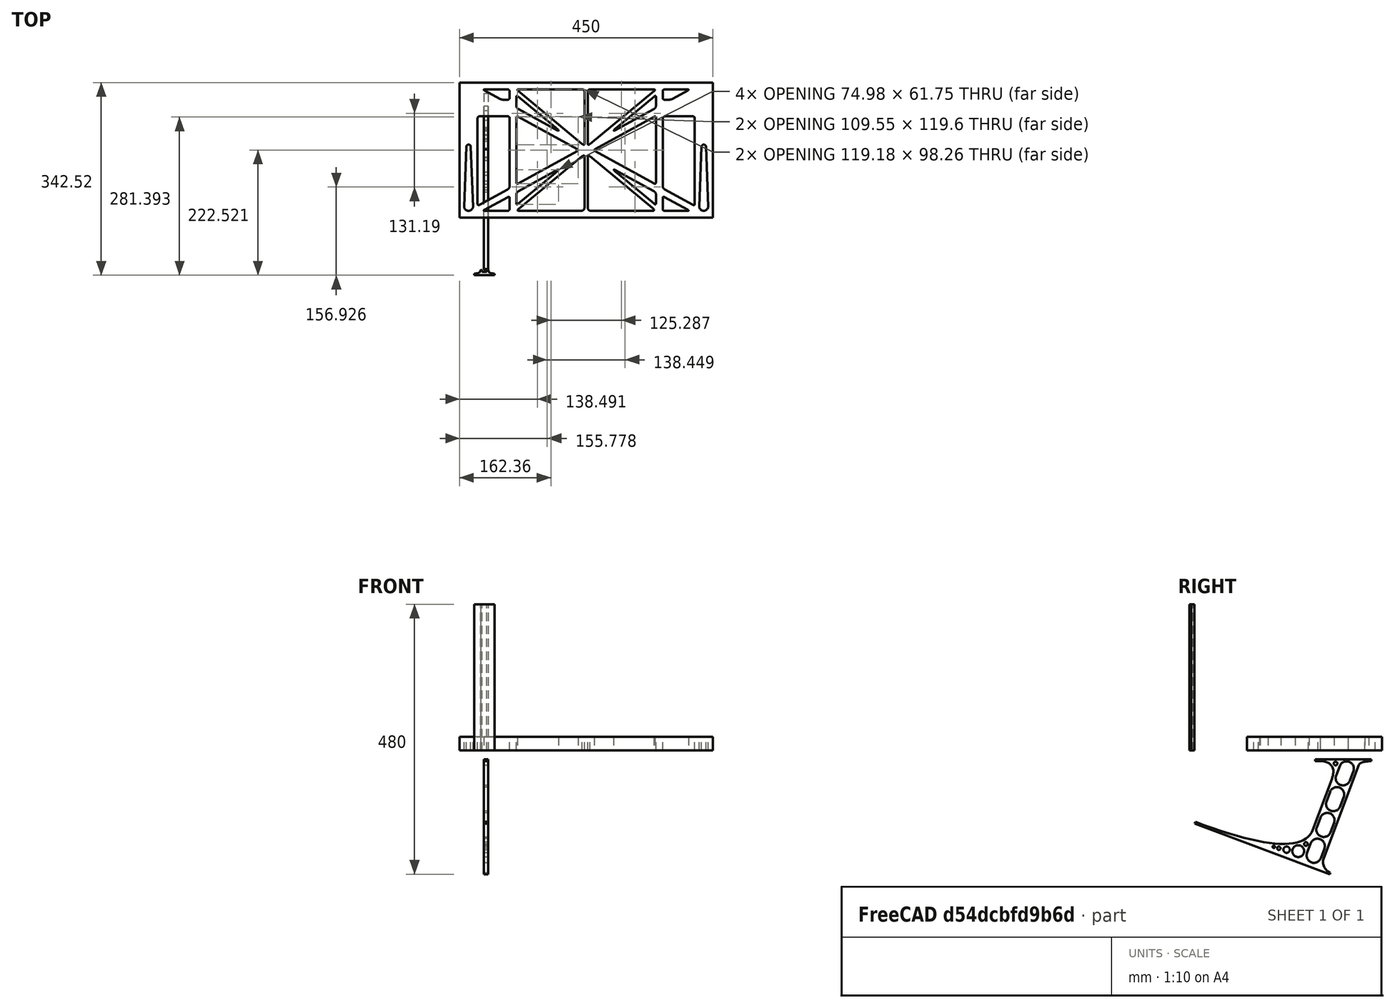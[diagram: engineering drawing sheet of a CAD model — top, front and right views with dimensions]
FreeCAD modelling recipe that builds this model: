
FCSTD DOCUMENT  (FreeCAD 0.19R0.19.2)
Label: laptopStand173FCStd
License: All rights reserved
LicenseURL: http://en.wikipedia.org/wiki/All_rights_reserved
objects: Sketcher::SketchObject×4, Part::Extrusion×3
note: 7 computed .brp shape members not serialized (recipe doc carries the construction recipe); baked Part::Feature solids carry a one-line shape summary decoded from their .brp

FEATURE [Sketcher::SketchObject] Sketch
  FullyConstrained = false
  sketch-geometry (349):
    g0: LineSegment StartX=-10.9272 StartY=-82.7794 StartZ=0 EndX=46.0728 EndY=-51.4823 EndZ=0
    g1: LineSegment StartX=-10.9272 StartY=76.4095 StartZ=0 EndX=-10.9272 EndY=-82.7794 EndZ=0
    g2: LineSegment StartX=46.0728 StartY=76.4095 StartZ=0 EndX=46.0728 EndY=-51.4823 EndZ=0
    g3: LineSegment StartX=-42.9272 StartY=136.221 StartZ=0 EndX=-42.9272 EndY=-103.779 EndZ=0
    g4: LineSegment StartX=407.073 StartY=136.221 StartZ=0 EndX=407.073 EndY=-103.779 EndZ=0
    g5: ArcOfCircle CenterX=-26.9272 CenterY=-83.7794 CenterZ=0 NormalX=0 NormalY=0 NormalZ=1 AngleXU=0 Radius=8 StartAngle=3.14159 EndAngle=6.28319
    g6: ArcOfCircle CenterX=391.073 CenterY=22.1087 CenterZ=0 NormalX=0 NormalY=0 NormalZ=1 AngleXU=0 Radius=8 StartAngle=-4.4e-15 EndAngle=3.14159
    g7: LineSegment StartX=399.073 StartY=22.1087 StartZ=0 EndX=399.073 EndY=-83.7794 EndZ=0
    g8: LineSegment StartX=383.073 StartY=22.1087 StartZ=0 EndX=383.073 EndY=-83.7794 EndZ=0
    g9: ArcOfCircle CenterX=391.073 CenterY=-83.7794 CenterZ=0 NormalX=0 NormalY=0 NormalZ=1 AngleXU=0 Radius=8 StartAngle=3.14159 EndAngle=6.28319
    g10: Circle CenterX=175.022 CenterY=27.0628 CenterZ=0 NormalX=0 NormalY=0 NormalZ=1 AngleXU=0 Radius=1
    g11: Circle CenterX=179.022 CenterY=24.8665 CenterZ=0 NormalX=0 NormalY=0 NormalZ=1 AngleXU=0 Radius=1
    g12: Circle CenterX=179.022 CenterY=27.0628 CenterZ=0 NormalX=0 NormalY=0 NormalZ=1 AngleXU=0 Radius=1
    g13: BSplineCurve PolesCount=3 KnotsCount=2 Degree=2 IsPeriodic=0
    g14: GeomPoint X=175.022 Y=27.0628 Z=0
    g15: GeomPoint X=179.022 Y=27.0628 Z=0
    g16: Circle CenterX=189.124 CenterY=27.0628 CenterZ=0 NormalX=0 NormalY=0 NormalZ=1 AngleXU=0 Radius=1
    g17: Circle CenterX=185.124 CenterY=24.8665 CenterZ=0 NormalX=0 NormalY=0 NormalZ=1 AngleXU=0 Radius=1
    g18: Circle CenterX=185.124 CenterY=27.0628 CenterZ=0 NormalX=0 NormalY=0 NormalZ=1 AngleXU=0 Radius=1
    g19: BSplineCurve PolesCount=3 KnotsCount=2 Degree=2 IsPeriodic=0
    g20: GeomPoint X=189.124 Y=27.0628 Z=0
    g21: GeomPoint X=185.124 Y=27.0628 Z=0
    g22: Circle CenterX=175.022 CenterY=5.37834 CenterZ=0 NormalX=0 NormalY=0 NormalZ=1 AngleXU=0 Radius=1
    g23: Circle CenterX=179.022 CenterY=7.57463 CenterZ=0 NormalX=0 NormalY=0 NormalZ=1 AngleXU=0 Radius=1
    g24: Circle CenterX=179.022 CenterY=5.34704 CenterZ=0 NormalX=0 NormalY=0 NormalZ=1 AngleXU=0 Radius=1
    g25: BSplineCurve PolesCount=3 KnotsCount=2 Degree=2 IsPeriodic=0
    g26: GeomPoint X=175.022 Y=5.37834 Z=0
    g27: GeomPoint X=179.022 Y=5.34704 Z=0
    g28: Circle CenterX=189.124 CenterY=5.37834 CenterZ=0 NormalX=0 NormalY=0 NormalZ=1 AngleXU=0 Radius=1
    g29: Circle CenterX=185.124 CenterY=7.57463 CenterZ=0 NormalX=0 NormalY=0 NormalZ=1 AngleXU=0 Radius=1
    g30: Circle CenterX=185.124 CenterY=5.34704 CenterZ=0 NormalX=0 NormalY=0 NormalZ=1 AngleXU=0 Radius=1
    g31: BSplineCurve PolesCount=3 KnotsCount=2 Degree=2 IsPeriodic=0
    g32: GeomPoint X=189.124 Y=5.37834 Z=0
    g33: GeomPoint X=185.124 Y=5.34704 Z=0
    g34: Circle CenterX=165.871 CenterY=18.1458 CenterZ=0 NormalX=0 NormalY=0 NormalZ=1 AngleXU=0 Radius=1
    g35: Circle CenterX=169.377 CenterY=16.2206 CenterZ=0 NormalX=0 NormalY=0 NormalZ=1 AngleXU=0 Radius=1
    g36: Circle CenterX=165.871 CenterY=14.2954 CenterZ=0 NormalX=0 NormalY=0 NormalZ=1 AngleXU=0 Radius=1
    g37: BSplineCurve PolesCount=3 KnotsCount=2 Degree=2 IsPeriodic=0
    g38: GeomPoint X=165.871 Y=18.1458 Z=0
    g39: GeomPoint X=165.871 Y=14.2954 Z=0
    g40: Circle CenterX=198.275 CenterY=18.1458 CenterZ=0 NormalX=0 NormalY=0 NormalZ=1 AngleXU=0 Radius=1
    g41: Circle CenterX=194.768 CenterY=16.2206 CenterZ=0 NormalX=0 NormalY=0 NormalZ=1 AngleXU=0 Radius=1
    g42: Circle CenterX=198.275 CenterY=14.2954 CenterZ=0 NormalX=0 NormalY=0 NormalZ=1 AngleXU=0 Radius=1
    g43: BSplineCurve PolesCount=3 KnotsCount=2 Degree=2 IsPeriodic=0
    g44: GeomPoint X=198.275 Y=18.1458 Z=0
    g45: GeomPoint X=198.275 Y=14.2954 Z=0
    g46: LineSegment StartX=407.073 StartY=-103.779 StartZ=0 EndX=-42.9272 EndY=-103.779 EndZ=0
    g47: LineSegment StartX=407.073 StartY=136.221 StartZ=0 EndX=-42.9272 EndY=136.221 EndZ=0
    g48: LineSegment StartX=46.0728 StartY=76.4095 StartZ=0 EndX=-10.9272 EndY=76.4095 EndZ=0
    g49: Circle CenterX=125.607 CenterY=54.1951 CenterZ=0 NormalX=0 NormalY=0 NormalZ=1 AngleXU=0 Radius=1
    g50: Circle CenterX=139.632 CenterY=46.4944 CenterZ=0 NormalX=0 NormalY=0 NormalZ=1 AngleXU=0 Radius=1
    g51: Circle CenterX=127.326 CenterY=56.7187 CenterZ=0 NormalX=0 NormalY=0 NormalZ=1 AngleXU=0 Radius=1
    g52: BSplineCurve PolesCount=3 KnotsCount=2 Degree=2 IsPeriodic=0
    g53: GeomPoint X=125.607 Y=54.1951 Z=0
    g54: GeomPoint X=127.326 Y=56.7187 Z=0
    g55: Circle CenterX=236.821 CenterY=56.7187 CenterZ=0 NormalX=0 NormalY=0 NormalZ=1 AngleXU=0 Radius=1
    g56: Circle CenterX=224.513 CenterY=46.4944 CenterZ=0 NormalX=0 NormalY=0 NormalZ=1 AngleXU=0 Radius=1
    g57: Circle CenterX=238.538 CenterY=54.1951 CenterZ=0 NormalX=0 NormalY=0 NormalZ=1 AngleXU=0 Radius=1
    g58: BSplineCurve PolesCount=3 KnotsCount=2 Degree=2 IsPeriodic=0
    g59: GeomPoint X=236.821 Y=56.7187 Z=0
    g60: GeomPoint X=238.538 Y=54.1951 Z=0
    g61: Circle CenterX=238.538 CenterY=-21.7539 CenterZ=0 NormalX=0 NormalY=0 NormalZ=1 AngleXU=0 Radius=1
    g62: Circle CenterX=224.513 CenterY=-14.0532 CenterZ=0 NormalX=0 NormalY=0 NormalZ=1 AngleXU=0 Radius=1
    g63: Circle CenterX=236.821 CenterY=-24.2775 CenterZ=0 NormalX=0 NormalY=0 NormalZ=1 AngleXU=0 Radius=1
    g64: BSplineCurve PolesCount=3 KnotsCount=2 Degree=2 IsPeriodic=0
    g65: GeomPoint X=238.538 Y=-21.7539 Z=0
    g66: GeomPoint X=236.821 Y=-24.2775 Z=0
    g67: Circle CenterX=125.607 CenterY=-21.7539 CenterZ=0 NormalX=0 NormalY=0 NormalZ=1 AngleXU=0 Radius=1
    g68: Circle CenterX=139.632 CenterY=-14.0532 CenterZ=0 NormalX=0 NormalY=0 NormalZ=1 AngleXU=0 Radius=1
    g69: Circle CenterX=127.325 CenterY=-24.2775 CenterZ=0 NormalX=0 NormalY=0 NormalZ=1 AngleXU=0 Radius=1
    g70: BSplineCurve PolesCount=3 KnotsCount=2 Degree=2 IsPeriodic=0
    g71: GeomPoint X=125.607 Y=-21.7539 Z=0
    g72: GeomPoint X=127.325 Y=-24.2775 Z=0
    g73: Circle CenterX=302.996 CenterY=111.695 CenterZ=0 NormalX=0 NormalY=0 NormalZ=1 AngleXU=0 Radius=1
    g74: Circle CenterX=306.073 CenterY=114.251 CenterZ=0 NormalX=0 NormalY=0 NormalZ=1 AngleXU=0 Radius=1
    g75: Circle CenterX=306.073 CenterY=110.251 CenterZ=0 NormalX=0 NormalY=0 NormalZ=1 AngleXU=0 Radius=1
    g76: BSplineCurve PolesCount=3 KnotsCount=2 Degree=2 IsPeriodic=0
    g77: GeomPoint X=302.996 Y=111.695 Z=0
    g78: GeomPoint X=306.073 Y=110.251 Z=0
    g79: Circle CenterX=306.073 CenterY=95.2763 CenterZ=0 NormalX=0 NormalY=0 NormalZ=1 AngleXU=0 Radius=1
    g80: Circle CenterX=306.073 CenterY=91.2763 CenterZ=0 NormalX=0 NormalY=0 NormalZ=1 AngleXU=0 Radius=1
    g81: Circle CenterX=302.567 CenterY=89.3511 CenterZ=0 NormalX=0 NormalY=0 NormalZ=1 AngleXU=0 Radius=1
    g82: BSplineCurve PolesCount=3 KnotsCount=2 Degree=2 IsPeriodic=0
    g83: GeomPoint X=306.073 Y=95.2763 Z=0
    g84: GeomPoint X=302.567 Y=89.3511 Z=0
    g85: LineSegment StartX=306.073 StartY=110.251 StartZ=0 EndX=306.073 EndY=95.2763 EndZ=0
    g86: LineSegment StartX=302.996 StartY=111.695 StartZ=0 EndX=236.821 EndY=56.7187 EndZ=0
    g87: LineSegment StartX=238.538 StartY=54.1951 StartZ=0 EndX=302.567 EndY=89.3511 EndZ=0
    g88: Circle CenterX=61.1496 CenterY=111.695 CenterZ=0 NormalX=0 NormalY=0 NormalZ=1 AngleXU=0 Radius=1
    g89: Circle CenterX=58.0728 CenterY=114.251 CenterZ=0 NormalX=0 NormalY=0 NormalZ=1 AngleXU=0 Radius=1
    g90: Circle CenterX=58.0728 CenterY=110.251 CenterZ=0 NormalX=0 NormalY=0 NormalZ=1 AngleXU=0 Radius=1
    g91: BSplineCurve PolesCount=3 KnotsCount=2 Degree=2 IsPeriodic=0
    g92: GeomPoint X=61.1496 Y=111.695 Z=0
    g93: GeomPoint X=58.0728 Y=110.251 Z=0
    g94: Circle CenterX=61.5791 CenterY=89.3511 CenterZ=0 NormalX=0 NormalY=0 NormalZ=1 AngleXU=0 Radius=1
    g95: Circle CenterX=58.0728 CenterY=91.2763 CenterZ=0 NormalX=0 NormalY=0 NormalZ=1 AngleXU=0 Radius=1
    g96: Circle CenterX=58.0728 CenterY=95.2763 CenterZ=0 NormalX=0 NormalY=0 NormalZ=1 AngleXU=0 Radius=1
    g97: BSplineCurve PolesCount=3 KnotsCount=2 Degree=2 IsPeriodic=0
    g98: GeomPoint X=61.5791 Y=89.3511 Z=0
    g99: GeomPoint X=58.0728 Y=95.2763 Z=0
    g100: LineSegment StartX=58.0728 StartY=110.251 StartZ=0 EndX=58.0728 EndY=95.2763 EndZ=0
    g101: LineSegment StartX=61.1496 StartY=111.695 StartZ=0 EndX=127.326 EndY=56.7187 EndZ=0
    g102: LineSegment StartX=125.607 StartY=54.1951 StartZ=0 EndX=61.5791 EndY=89.3511 EndZ=0
    g103: Circle CenterX=61.5791 CenterY=-56.9099 CenterZ=0 NormalX=0 NormalY=0 NormalZ=1 AngleXU=0 Radius=1
    g104: Circle CenterX=58.0728 CenterY=-58.8351 CenterZ=0 NormalX=0 NormalY=0 NormalZ=1 AngleXU=0 Radius=1
    g105: Circle CenterX=58.0728 CenterY=-62.8351 CenterZ=0 NormalX=0 NormalY=0 NormalZ=1 AngleXU=0 Radius=1
    g106: BSplineCurve PolesCount=3 KnotsCount=2 Degree=2 IsPeriodic=0
    g107: GeomPoint X=61.5791 Y=-56.9099 Z=0
    g108: GeomPoint X=58.0728 Y=-62.8351 Z=0
    g109: Circle CenterX=58.0728 CenterY=-77.8102 CenterZ=0 NormalX=0 NormalY=0 NormalZ=1 AngleXU=0 Radius=1
    g110: Circle CenterX=58.0728 CenterY=-81.8102 CenterZ=0 NormalX=0 NormalY=0 NormalZ=1 AngleXU=0 Radius=1
    g111: Circle CenterX=61.1496 CenterY=-79.2541 CenterZ=0 NormalX=0 NormalY=0 NormalZ=1 AngleXU=0 Radius=1
    g112: BSplineCurve PolesCount=3 KnotsCount=2 Degree=2 IsPeriodic=0
    g113: GeomPoint X=58.0728 Y=-77.8102 Z=0
    g114: GeomPoint X=61.1496 Y=-79.2541 Z=0
    g115: LineSegment StartX=58.0728 StartY=-62.8351 StartZ=0 EndX=58.0728 EndY=-77.8102 EndZ=0
    g116: LineSegment StartX=61.1496 StartY=-79.2541 StartZ=0 EndX=127.325 EndY=-24.2775 EndZ=0
    g117: LineSegment StartX=125.607 StartY=-21.7539 StartZ=0 EndX=61.5791 EndY=-56.9099 EndZ=0
    g118: Circle CenterX=302.567 CenterY=-56.9099 CenterZ=0 NormalX=0 NormalY=0 NormalZ=1 AngleXU=0 Radius=1
    g119: Circle CenterX=306.073 CenterY=-58.8351 CenterZ=0 NormalX=0 NormalY=0 NormalZ=1 AngleXU=0 Radius=1
    g120: Circle CenterX=306.073 CenterY=-62.8351 CenterZ=0 NormalX=0 NormalY=0 NormalZ=1 AngleXU=0 Radius=1
    g121: BSplineCurve PolesCount=3 KnotsCount=2 Degree=2 IsPeriodic=0
    g122: GeomPoint X=302.567 Y=-56.9099 Z=0
    g123: GeomPoint X=306.073 Y=-62.8351 Z=0
    g124: Circle CenterX=302.996 CenterY=-79.2541 CenterZ=0 NormalX=0 NormalY=0 NormalZ=1 AngleXU=0 Radius=1
    g125: Circle CenterX=306.073 CenterY=-81.8102 CenterZ=0 NormalX=0 NormalY=0 NormalZ=1 AngleXU=0 Radius=1
    g126: Circle CenterX=306.073 CenterY=-77.8102 CenterZ=0 NormalX=0 NormalY=0 NormalZ=1 AngleXU=0 Radius=1
    g127: BSplineCurve PolesCount=3 KnotsCount=2 Degree=2 IsPeriodic=0
    g128: GeomPoint X=302.996 Y=-79.2541 Z=0
    g129: GeomPoint X=306.073 Y=-77.8102 Z=0
    g130: LineSegment StartX=306.073 StartY=-62.8351 StartZ=0 EndX=306.073 EndY=-77.8102 EndZ=0
    g131: LineSegment StartX=302.996 StartY=-79.2541 StartZ=0 EndX=236.821 EndY=-24.2775 EndZ=0
    g132: LineSegment StartX=238.538 StartY=-21.7539 StartZ=0 EndX=302.567 EndY=-56.9099 EndZ=0
    g133: Circle CenterX=61.6457 CenterY=-88.8112 CenterZ=0 NormalX=0 NormalY=0 NormalZ=1 AngleXU=0 Radius=1
    g134: Circle CenterX=58.0728 CenterY=-91.7794 CenterZ=0 NormalX=0 NormalY=0 NormalZ=1 AngleXU=0 Radius=1
    g135: Circle CenterX=63.9135 CenterY=-91.7794 CenterZ=0 NormalX=0 NormalY=0 NormalZ=1 AngleXU=0 Radius=1
    g136: BSplineCurve PolesCount=3 KnotsCount=2 Degree=2 IsPeriodic=0
    g137: GeomPoint X=61.6457 Y=-88.8112 Z=0
    g138: GeomPoint X=63.9135 Y=-91.7794 Z=0
    g139: Circle CenterX=179.022 CenterY=-85.8163 CenterZ=0 NormalX=0 NormalY=0 NormalZ=1 AngleXU=0 Radius=1
    g140: Circle CenterX=179.022 CenterY=-91.7794 CenterZ=0 NormalX=0 NormalY=0 NormalZ=1 AngleXU=0 Radius=1
    g141: Circle CenterX=171.895 CenterY=-91.7794 CenterZ=0 NormalX=0 NormalY=0 NormalZ=1 AngleXU=0 Radius=1
    g142: BSplineCurve PolesCount=3 KnotsCount=2 Degree=2 IsPeriodic=0
    g143: GeomPoint X=179.022 Y=-85.8163 Z=0
    g144: GeomPoint X=171.895 Y=-91.7794 Z=0
    g145: Circle CenterX=185.124 CenterY=-86.2028 CenterZ=0 NormalX=0 NormalY=0 NormalZ=1 AngleXU=0 Radius=1
    g146: Circle CenterX=185.124 CenterY=-91.7794 CenterZ=0 NormalX=0 NormalY=0 NormalZ=1 AngleXU=0 Radius=1
    g147: Circle CenterX=191.747 CenterY=-91.7794 CenterZ=0 NormalX=0 NormalY=0 NormalZ=1 AngleXU=0 Radius=1
    g148: BSplineCurve PolesCount=3 KnotsCount=2 Degree=2 IsPeriodic=0
    g149: GeomPoint X=185.124 Y=-86.2028 Z=0
    g150: GeomPoint X=191.747 Y=-91.7794 Z=0
    g151: Circle CenterX=299.888 CenterY=-86.6413 CenterZ=0 NormalX=0 NormalY=0 NormalZ=1 AngleXU=0 Radius=1
    g152: Circle CenterX=306.073 CenterY=-91.7794 CenterZ=0 NormalX=0 NormalY=0 NormalZ=1 AngleXU=0 Radius=1
    g153: Circle CenterX=298.776 CenterY=-91.7794 CenterZ=0 NormalX=0 NormalY=0 NormalZ=1 AngleXU=0 Radius=1
    g154: BSplineCurve PolesCount=3 KnotsCount=2 Degree=2 IsPeriodic=0
    g155: GeomPoint X=299.888 Y=-86.6413 Z=0
    g156: GeomPoint X=298.776 Y=-91.7794 Z=0
    g157: LineSegment StartX=189.124 StartY=5.37834 StartZ=0 EndX=299.888 EndY=-86.6413 EndZ=0
    g158: LineSegment StartX=298.776 StartY=-91.7794 StartZ=0 EndX=191.747 EndY=-91.7794 EndZ=0
    g159: LineSegment StartX=185.124 StartY=-86.2028 StartZ=0 EndX=185.124 EndY=5.34704 EndZ=0
    g160: LineSegment StartX=179.022 StartY=5.34704 StartZ=0 EndX=179.022 EndY=-85.8163 EndZ=0
    g161: LineSegment StartX=171.895 StartY=-91.7794 StartZ=0 EndX=63.9135 EndY=-91.7794 EndZ=0
    g162: LineSegment StartX=61.6457 StartY=-88.8112 StartZ=0 EndX=175.022 EndY=5.37834 EndZ=0
    g163: Circle CenterX=302.073 CenterY=124.221 CenterZ=0 NormalX=0 NormalY=0 NormalZ=1 AngleXU=0 Radius=1
    g164: Circle CenterX=306.073 CenterY=124.221 CenterZ=0 NormalX=0 NormalY=0 NormalZ=1 AngleXU=0 Radius=1
    g165: Circle CenterX=302.996 CenterY=121.665 CenterZ=0 NormalX=0 NormalY=0 NormalZ=1 AngleXU=0 Radius=1
    g166: BSplineCurve PolesCount=3 KnotsCount=2 Degree=2 IsPeriodic=0
    g167: GeomPoint X=302.073 Y=124.221 Z=0
    g168: GeomPoint X=302.996 Y=121.665 Z=0
    g169: Circle CenterX=189.124 CenterY=124.221 CenterZ=0 NormalX=0 NormalY=0 NormalZ=1 AngleXU=0 Radius=1
    g170: Circle CenterX=185.124 CenterY=124.221 CenterZ=0 NormalX=0 NormalY=0 NormalZ=1 AngleXU=0 Radius=1
    g171: Circle CenterX=185.124 CenterY=120.221 CenterZ=0 NormalX=0 NormalY=0 NormalZ=1 AngleXU=0 Radius=1
    g172: BSplineCurve PolesCount=3 KnotsCount=2 Degree=2 IsPeriodic=0
    g173: GeomPoint X=189.124 Y=124.221 Z=0
    g174: GeomPoint X=185.124 Y=120.221 Z=0
    g175: Circle CenterX=175.022 CenterY=124.221 CenterZ=0 NormalX=0 NormalY=0 NormalZ=1 AngleXU=0 Radius=1
    g176: Circle CenterX=179.022 CenterY=124.221 CenterZ=0 NormalX=0 NormalY=0 NormalZ=1 AngleXU=0 Radius=1
    g177: Circle CenterX=179.022 CenterY=120.221 CenterZ=0 NormalX=0 NormalY=0 NormalZ=1 AngleXU=0 Radius=1
    g178: BSplineCurve PolesCount=3 KnotsCount=2 Degree=2 IsPeriodic=0
    g179: GeomPoint X=175.022 Y=124.221 Z=0
    g180: GeomPoint X=179.022 Y=120.221 Z=0
    g181: Circle CenterX=62.0728 CenterY=124.221 CenterZ=0 NormalX=0 NormalY=0 NormalZ=1 AngleXU=0 Radius=1
    g182: Circle CenterX=58.0728 CenterY=124.221 CenterZ=0 NormalX=0 NormalY=0 NormalZ=1 AngleXU=0 Radius=1
    g183: Circle CenterX=61.1496 CenterY=121.665 CenterZ=0 NormalX=0 NormalY=0 NormalZ=1 AngleXU=0 Radius=1
    g184: BSplineCurve PolesCount=3 KnotsCount=2 Degree=2 IsPeriodic=0
    g185: GeomPoint X=62.0728 Y=124.221 Z=0
    g186: GeomPoint X=61.1496 Y=121.665 Z=0
    g187: LineSegment StartX=62.0728 StartY=124.221 StartZ=0 EndX=175.022 EndY=124.221 EndZ=0
    g188: LineSegment StartX=179.022 StartY=120.221 StartZ=0 EndX=179.022 EndY=27.0628 EndZ=0
    g189: LineSegment StartX=185.124 StartY=27.0628 StartZ=0 EndX=185.124 EndY=120.221 EndZ=0
    g190: LineSegment StartX=189.124 StartY=124.221 StartZ=0 EndX=302.073 EndY=124.221 EndZ=0
    g191: LineSegment StartX=302.996 StartY=121.665 StartZ=0 EndX=189.124 EndY=27.0628 EndZ=0
    g192: LineSegment StartX=175.022 StartY=27.0628 StartZ=0 EndX=61.1496 EndY=121.665 EndZ=0
    g193: Circle CenterX=61.5791 CenterY=75.4095 CenterZ=0 NormalX=0 NormalY=0 NormalZ=1 AngleXU=0 Radius=1
    g194: Circle CenterX=58.0728 CenterY=77.3346 CenterZ=0 NormalX=0 NormalY=0 NormalZ=1 AngleXU=0 Radius=1
    g195: Circle CenterX=58.0728 CenterY=73.3346 CenterZ=0 NormalX=0 NormalY=0 NormalZ=1 AngleXU=0 Radius=1
    g196: BSplineCurve PolesCount=3 KnotsCount=2 Degree=2 IsPeriodic=0
    g197: GeomPoint X=61.5791 Y=75.4095 Z=0
    g198: GeomPoint X=58.0728 Y=73.3346 Z=0
    g199: Circle CenterX=58.0728 CenterY=-40.8935 CenterZ=0 NormalX=0 NormalY=0 NormalZ=1 AngleXU=0 Radius=1
    g200: Circle CenterX=58.0728 CenterY=-44.8935 CenterZ=0 NormalX=0 NormalY=0 NormalZ=1 AngleXU=0 Radius=1
    g201: Circle CenterX=61.5791 CenterY=-42.9683 CenterZ=0 NormalX=0 NormalY=0 NormalZ=1 AngleXU=0 Radius=1
    g202: BSplineCurve PolesCount=3 KnotsCount=2 Degree=2 IsPeriodic=0
    g203: GeomPoint X=58.0728 Y=-40.8935 Z=0
    g204: GeomPoint X=61.5791 Y=-42.9683 Z=0
    g205: LineSegment StartX=61.5791 StartY=-42.9683 StartZ=0 EndX=165.871 EndY=14.2954 EndZ=0
    g206: LineSegment StartX=165.871 StartY=18.1458 StartZ=0 EndX=61.5791 EndY=75.4095 EndZ=0
    g207: LineSegment StartX=58.0728 StartY=73.3346 StartZ=0 EndX=58.0728 EndY=-40.8935 EndZ=0
    g208: Circle CenterX=302.567 CenterY=-42.9683 CenterZ=0 NormalX=0 NormalY=0 NormalZ=1 AngleXU=0 Radius=1
    g209: Circle CenterX=306.073 CenterY=-44.8935 CenterZ=0 NormalX=0 NormalY=0 NormalZ=1 AngleXU=0 Radius=1
    g210: Circle CenterX=306.073 CenterY=-40.8935 CenterZ=0 NormalX=0 NormalY=0 NormalZ=1 AngleXU=0 Radius=1
    g211: BSplineCurve PolesCount=3 KnotsCount=2 Degree=2 IsPeriodic=0
    g212: GeomPoint X=302.567 Y=-42.9683 Z=0
    g213: GeomPoint X=306.073 Y=-40.8935 Z=0
    g214: Circle CenterX=306.073 CenterY=73.3346 CenterZ=0 NormalX=0 NormalY=0 NormalZ=1 AngleXU=0 Radius=1
    g215: Circle CenterX=306.073 CenterY=77.3346 CenterZ=0 NormalX=0 NormalY=0 NormalZ=1 AngleXU=0 Radius=1
    g216: Circle CenterX=302.567 CenterY=75.4095 CenterZ=0 NormalX=0 NormalY=0 NormalZ=1 AngleXU=0 Radius=1
    g217: BSplineCurve PolesCount=3 KnotsCount=2 Degree=2 IsPeriodic=0
    g218: GeomPoint X=306.073 Y=73.3346 Z=0
    g219: GeomPoint X=302.567 Y=75.4095 Z=0
    g220: LineSegment StartX=302.567 StartY=-42.9683 StartZ=0 EndX=198.275 EndY=14.2954 EndZ=0
    g221: LineSegment StartX=198.275 StartY=18.1458 StartZ=0 EndX=302.567 EndY=75.4095 EndZ=0
    g222: LineSegment StartX=306.073 StartY=73.3346 StartZ=0 EndX=306.073 EndY=-40.8935 EndZ=0
    g223: LineSegment StartX=322.073 StartY=105.865 StartZ=0 EndX=328.643 EndY=105.865 EndZ=0
    g224: LineSegment StartX=318.073 StartY=120.221 StartZ=0 EndX=318.073 EndY=109.865 EndZ=0
    g225: LineSegment StartX=336.157 StartY=107.779 StartZ=0 EndX=362.567 EndY=122.294 EndZ=0
    g226: Circle CenterX=362.073 CenterY=124.221 CenterZ=0 NormalX=0 NormalY=0 NormalZ=1 AngleXU=0 Radius=1
    g227: Circle CenterX=366.073 CenterY=124.221 CenterZ=0 NormalX=0 NormalY=0 NormalZ=1 AngleXU=0 Radius=1
    g228: Circle CenterX=362.567 CenterY=122.294 CenterZ=0 NormalX=0 NormalY=0 NormalZ=1 AngleXU=0 Radius=1
    g229: BSplineCurve PolesCount=3 KnotsCount=2 Degree=2 IsPeriodic=0
    g230: GeomPoint X=362.073 Y=124.221 Z=0
    g231: GeomPoint X=362.567 Y=122.294 Z=0
    g232: Circle CenterX=322.073 CenterY=124.221 CenterZ=0 NormalX=0 NormalY=0 NormalZ=1 AngleXU=0 Radius=1
    g233: Circle CenterX=318.073 CenterY=124.221 CenterZ=0 NormalX=0 NormalY=0 NormalZ=1 AngleXU=0 Radius=1
    g234: Circle CenterX=318.073 CenterY=120.221 CenterZ=0 NormalX=0 NormalY=0 NormalZ=1 AngleXU=0 Radius=1
    g235: BSplineCurve PolesCount=3 KnotsCount=2 Degree=2 IsPeriodic=0
    g236: GeomPoint X=322.073 Y=124.221 Z=0
    g237: GeomPoint X=318.073 Y=120.221 Z=0
    g238: Circle CenterX=322.073 CenterY=105.865 CenterZ=0 NormalX=0 NormalY=0 NormalZ=1 AngleXU=0 Radius=1
    g239: Circle CenterX=318.073 CenterY=105.865 CenterZ=0 NormalX=0 NormalY=0 NormalZ=1 AngleXU=0 Radius=1
    g240: Circle CenterX=318.073 CenterY=109.865 CenterZ=0 NormalX=0 NormalY=0 NormalZ=1 AngleXU=0 Radius=1
    g241: BSplineCurve PolesCount=3 KnotsCount=2 Degree=2 IsPeriodic=0
    g242: GeomPoint X=322.073 Y=105.865 Z=0
    g243: GeomPoint X=318.073 Y=109.865 Z=0
    g244: Circle CenterX=336.157 CenterY=107.779 CenterZ=0 NormalX=0 NormalY=0 NormalZ=1 AngleXU=0 Radius=1
    g245: Circle CenterX=332.651 CenterY=105.853 CenterZ=0 NormalX=0 NormalY=0 NormalZ=1 AngleXU=0 Radius=1
    g246: Circle CenterX=328.643 CenterY=105.865 CenterZ=0 NormalX=0 NormalY=0 NormalZ=1 AngleXU=0 Radius=1
    g247: BSplineCurve PolesCount=3 KnotsCount=2 Degree=2 IsPeriodic=0
    g248: GeomPoint X=336.157 Y=107.779 Z=0
    g249: GeomPoint X=328.643 Y=105.865 Z=0
    g250: LineSegment StartX=322.073 StartY=124.221 StartZ=0 EndX=362.073 EndY=124.221 EndZ=0
    g251: Circle CenterX=371.567 CenterY=-80.8644 CenterZ=0 NormalX=0 NormalY=0 NormalZ=1 AngleXU=0 Radius=1
    g252: Circle CenterX=375.073 CenterY=-82.7896 CenterZ=0 NormalX=0 NormalY=0 NormalZ=1 AngleXU=0 Radius=1
    g253: Circle CenterX=375.073 CenterY=-78.7896 CenterZ=0 NormalX=0 NormalY=0 NormalZ=1 AngleXU=0 Radius=1
    g254: BSplineCurve PolesCount=3 KnotsCount=2 Degree=2 IsPeriodic=0
    g255: GeomPoint X=371.567 Y=-80.8644 Z=0
    g256: GeomPoint X=375.073 Y=-78.7896 Z=0
    g257: Circle CenterX=321.579 CenterY=-53.4075 CenterZ=0 NormalX=0 NormalY=0 NormalZ=1 AngleXU=0 Radius=1
    g258: Circle CenterX=318.073 CenterY=-51.4823 CenterZ=0 NormalX=0 NormalY=0 NormalZ=1 AngleXU=0 Radius=1
    g259: Circle CenterX=318.073 CenterY=-47.4805 CenterZ=0 NormalX=0 NormalY=0 NormalZ=1 AngleXU=0 Radius=1
    g260: BSplineCurve PolesCount=3 KnotsCount=2 Degree=2 IsPeriodic=0
    g261: GeomPoint X=321.579 Y=-53.4075 Z=0
    g262: GeomPoint X=318.073 Y=-47.4805 Z=0
    g263: LineSegment StartX=371.567 StartY=-80.8644 StartZ=0 EndX=321.579 EndY=-53.4075 EndZ=0
    g264: Circle CenterX=321.579 CenterY=-67.3492 CenterZ=0 NormalX=0 NormalY=0 NormalZ=1 AngleXU=0 Radius=1
    g265: Circle CenterX=318.073 CenterY=-65.424 CenterZ=0 NormalX=0 NormalY=0 NormalZ=1 AngleXU=0 Radius=1
    g266: Circle CenterX=318.073 CenterY=-69.424 CenterZ=0 NormalX=0 NormalY=0 NormalZ=1 AngleXU=0 Radius=1
    g267: BSplineCurve PolesCount=3 KnotsCount=2 Degree=2 IsPeriodic=0
    g268: GeomPoint X=321.579 Y=-67.3492 Z=0
    g269: GeomPoint X=318.073 Y=-69.424 Z=0
    g270: Circle CenterX=362.567 CenterY=-89.8542 CenterZ=0 NormalX=0 NormalY=0 NormalZ=1 AngleXU=0 Radius=1
    g271: Circle CenterX=366.073 CenterY=-91.7794 CenterZ=0 NormalX=0 NormalY=0 NormalZ=1 AngleXU=0 Radius=1
    g272: Circle CenterX=362.073 CenterY=-91.7794 CenterZ=0 NormalX=0 NormalY=0 NormalZ=1 AngleXU=0 Radius=1
    g273: BSplineCurve PolesCount=3 KnotsCount=2 Degree=2 IsPeriodic=0
    g274: GeomPoint X=362.567 Y=-89.8542 Z=0
    g275: GeomPoint X=362.073 Y=-91.7794 Z=0
    g276: Circle CenterX=322.073 CenterY=-91.7794 CenterZ=0 NormalX=0 NormalY=0 NormalZ=1 AngleXU=0 Radius=1
    g277: Circle CenterX=318.073 CenterY=-91.7794 CenterZ=0 NormalX=0 NormalY=0 NormalZ=1 AngleXU=0 Radius=1
    g278: Circle CenterX=318.073 CenterY=-87.7794 CenterZ=0 NormalX=0 NormalY=0 NormalZ=1 AngleXU=0 Radius=1
    g279: BSplineCurve PolesCount=3 KnotsCount=2 Degree=2 IsPeriodic=0
    g280: GeomPoint X=322.073 Y=-91.7794 Z=0
    g281: GeomPoint X=318.073 Y=-87.7794 Z=0
    g282: LineSegment StartX=362.567 StartY=-89.8542 StartZ=0 EndX=321.579 EndY=-67.3492 EndZ=0
    g283: LineSegment StartX=318.073 StartY=-69.424 StartZ=0 EndX=318.073 EndY=-87.7794 EndZ=0
    g284: LineSegment StartX=322.073 StartY=-91.7794 StartZ=0 EndX=362.073 EndY=-91.7794 EndZ=0
    g285: Circle CenterX=2.07281 CenterY=124.221 CenterZ=0 NormalX=0 NormalY=0 NormalZ=1 AngleXU=0 Radius=1
    g286: Circle CenterX=1.57905 CenterY=122.295 CenterZ=0 NormalX=0 NormalY=0 NormalZ=1 AngleXU=0 Radius=1
    g287: BSplineCurve PolesCount=3 KnotsCount=2 Degree=2 IsPeriodic=0
    g288: GeomPoint X=2.07281 Y=124.221 Z=0
    g289: GeomPoint X=1.57905 Y=122.295 Z=0
    g290: Circle CenterX=42.0728 CenterY=124.221 CenterZ=0 NormalX=0 NormalY=0 NormalZ=1 AngleXU=0 Radius=1
    g291: Circle CenterX=46.0728 CenterY=124.221 CenterZ=0 NormalX=0 NormalY=0 NormalZ=1 AngleXU=0 Radius=1
    g292: Circle CenterX=46.0728 CenterY=120.221 CenterZ=0 NormalX=0 NormalY=0 NormalZ=1 AngleXU=0 Radius=1
    g293: BSplineCurve PolesCount=3 KnotsCount=2 Degree=2 IsPeriodic=0
    g294: GeomPoint X=42.0728 Y=124.221 Z=0
    g295: GeomPoint X=46.0728 Y=120.221 Z=0
    g296: Circle CenterX=46.0728 CenterY=109.865 CenterZ=0 NormalX=0 NormalY=0 NormalZ=1 AngleXU=0 Radius=1
    g297: Circle CenterX=46.0728 CenterY=105.865 CenterZ=0 NormalX=0 NormalY=0 NormalZ=1 AngleXU=0 Radius=1
    g298: Circle CenterX=42.0728 CenterY=105.865 CenterZ=0 NormalX=0 NormalY=0 NormalZ=1 AngleXU=0 Radius=1
    g299: BSplineCurve PolesCount=3 KnotsCount=2 Degree=2 IsPeriodic=0
    g300: GeomPoint X=46.0728 Y=109.865 Z=0
    g301: GeomPoint X=42.0728 Y=105.865 Z=0
    g302: Circle CenterX=35.5028 CenterY=105.865 CenterZ=0 NormalX=0 NormalY=0 NormalZ=1 AngleXU=0 Radius=1
    g303: Circle CenterX=31.5028 CenterY=105.865 CenterZ=0 NormalX=0 NormalY=0 NormalZ=1 AngleXU=0 Radius=1
    g304: Circle CenterX=27.9965 CenterY=107.79 CenterZ=0 NormalX=0 NormalY=0 NormalZ=1 AngleXU=0 Radius=1
    g305: BSplineCurve PolesCount=3 KnotsCount=2 Degree=2 IsPeriodic=0
    g306: GeomPoint X=35.5028 Y=105.865 Z=0
    g307: GeomPoint X=27.9965 Y=107.79 Z=0
    g308: LineSegment StartX=2.07281 StartY=124.221 StartZ=0 EndX=42.0728 EndY=124.221 EndZ=0
    g309: LineSegment StartX=46.0728 StartY=120.221 StartZ=0 EndX=46.0728 EndY=109.865 EndZ=0
    g310: LineSegment StartX=42.0728 StartY=105.865 StartZ=0 EndX=35.5028 EndY=105.865 EndZ=0
    g311: LineSegment StartX=27.9965 StartY=107.79 StartZ=0 EndX=1.57905 EndY=122.295 EndZ=0
    g312: Circle CenterX=42.5666 CenterY=-67.3492 CenterZ=0 NormalX=0 NormalY=0 NormalZ=1 AngleXU=0 Radius=1
    g313: Circle CenterX=46.0728 CenterY=-65.424 CenterZ=0 NormalX=0 NormalY=0 NormalZ=1 AngleXU=0 Radius=1
    g314: Circle CenterX=46.0728 CenterY=-69.424 CenterZ=0 NormalX=0 NormalY=0 NormalZ=1 AngleXU=0 Radius=1
    g315: BSplineCurve PolesCount=3 KnotsCount=2 Degree=2 IsPeriodic=0
    g316: GeomPoint X=42.5666 Y=-67.3492 Z=0
    g317: GeomPoint X=46.0728 Y=-69.424 Z=0
    g318: Circle CenterX=46.0728 CenterY=-87.7794 CenterZ=0 NormalX=0 NormalY=0 NormalZ=1 AngleXU=0 Radius=1
    g319: Circle CenterX=46.0728 CenterY=-91.7794 CenterZ=0 NormalX=0 NormalY=0 NormalZ=1 AngleXU=0 Radius=1
    g320: Circle CenterX=42.0728 CenterY=-91.7794 CenterZ=0 NormalX=0 NormalY=0 NormalZ=1 AngleXU=0 Radius=1
    g321: BSplineCurve PolesCount=3 KnotsCount=2 Degree=2 IsPeriodic=0
    g322: GeomPoint X=46.0728 Y=-87.7794 Z=0
    g323: GeomPoint X=42.0728 Y=-91.7794 Z=0
    g324: Circle CenterX=2.07281 CenterY=-91.7794 CenterZ=0 NormalX=0 NormalY=0 NormalZ=1 AngleXU=0 Radius=1
    g325: Circle CenterX=-1.92719 CenterY=-91.7794 CenterZ=0 NormalX=0 NormalY=0 NormalZ=1 AngleXU=0 Radius=1
    g326: Circle CenterX=1.57905 CenterY=-89.8542 CenterZ=0 NormalX=0 NormalY=0 NormalZ=1 AngleXU=0 Radius=1
    g327: BSplineCurve PolesCount=3 KnotsCount=2 Degree=2 IsPeriodic=0
    g328: GeomPoint X=2.07281 Y=-91.7794 Z=0
    g329: GeomPoint X=1.57905 Y=-89.8542 Z=0
    g330: LineSegment StartX=2.07281 StartY=-91.7794 StartZ=0 EndX=42.0728 EndY=-91.7794 EndZ=0
    g331: LineSegment StartX=46.0728 StartY=-87.7794 StartZ=0 EndX=46.0728 EndY=-69.424 EndZ=0
    g332: LineSegment StartX=42.5666 StartY=-67.3492 StartZ=0 EndX=1.57905 EndY=-89.8542 EndZ=0
    g333: Circle CenterX=322.073 CenterY=76.4095 CenterZ=0 NormalX=0 NormalY=0 NormalZ=1 AngleXU=0 Radius=4
    g334: BSplineCurve PolesCount=3 KnotsCount=2 Degree=2 IsPeriodic=0
    g335: GeomPoint X=318.073 Y=72.4095 Z=0
    g336: GeomPoint X=322.073 Y=76.4095 Z=0
    g337: Circle CenterX=375.073 CenterY=72.4095 CenterZ=0 NormalX=0 NormalY=0 NormalZ=1 AngleXU=0 Radius=1
    g338: Circle CenterX=375.073 CenterY=76.4095 CenterZ=0 NormalX=0 NormalY=0 NormalZ=1 AngleXU=0 Radius=1
    g339: Circle CenterX=371.073 CenterY=76.4095 CenterZ=0 NormalX=0 NormalY=0 NormalZ=1 AngleXU=0 Radius=1
    g340: BSplineCurve PolesCount=3 KnotsCount=2 Degree=2 IsPeriodic=0
    g341: GeomPoint X=375.073 Y=72.4095 Z=0
    g342: GeomPoint X=371.073 Y=76.4095 Z=0
    g343: LineSegment StartX=322.073 StartY=76.4095 StartZ=0 EndX=371.073 EndY=76.4095 EndZ=0
    g344: LineSegment StartX=318.073 StartY=72.4095 StartZ=0 EndX=318.073 EndY=-47.4805 EndZ=0
    g345: LineSegment StartX=375.073 StartY=72.4095 StartZ=0 EndX=375.073 EndY=-78.7896 EndZ=0
    g346: ArcOfCircle CenterX=-26.9272 CenterY=22.1087 CenterZ=0 NormalX=0 NormalY=0 NormalZ=1 AngleXU=0 Radius=4 StartAngle=5e-16 EndAngle=3.14159
    g347: LineSegment StartX=-30.9272 StartY=22.1087 StartZ=0 EndX=-34.9272 EndY=-83.7794 EndZ=0
    g348: LineSegment StartX=-18.9272 StartY=-83.7794 StartZ=0 EndX=-22.9272 EndY=22.1087 EndZ=0
  constraints (572):
    c: Coincident(g0,g2)
    c: Block(g0)
    c: Block(g1)
    c: Vertical(g3)
    c: Vertical(g4)
    c: Block(g4)
    c: Block(g3)
    c: Tangent(g6,g7) = 1.5708
    c: Tangent(g7,g9) = 1.5708
    c: Equal(g6,g9)
    c: Coincident(g8,g6)
    c: Coincident(g8,g9)
    c: Block(g7)
    c: Block(g8)
    c: Weight(g10) = 1
    c: Equal(g10,g11)
    c: Equal(g10,g12)
    c: InternalAlignment(g10,g13)
    c: InternalAlignment(g11,g13)
    c: InternalAlignment(g12,g13)
    c: InternalAlignment(g14,g13)
    c: InternalAlignment(g15,g13)
    c: Weight(g16) = 1
    c: Equal(g16,g17)
    c: Equal(g16,g18)
    c: InternalAlignment(g16,g19)
    c: InternalAlignment(g17,g19)
    c: InternalAlignment(g18,g19)
    c: InternalAlignment(g20,g19)
    c: InternalAlignment(g21,g19)
    c: Block(g19)
    c: Block(g13)
    c: Weight(g22) = 1
    c: Equal(g22,g23)
    c: Equal(g22,g24)
    c: InternalAlignment(g22,g25)
    c: InternalAlignment(g23,g25)
    c: InternalAlignment(g24,g25)
    c: InternalAlignment(g26,g25)
    c: InternalAlignment(g27,g25)
    c: Weight(g28) = 1
    c: Equal(g28,g29)
    c: Equal(g28,g30)
    c: InternalAlignment(g28,g31)
    c: InternalAlignment(g29,g31)
    c: InternalAlignment(g30,g31)
    c: InternalAlignment(g32,g31)
    c: InternalAlignment(g33,g31)
    c: Block(g31)
    c: Block(g25)
    c: Weight(g34) = 1
    c: Equal(g34,g35)
    c: Equal(g34,g36)
    c: InternalAlignment(g34,g37)
    c: InternalAlignment(g35,g37)
    c: InternalAlignment(g36,g37)
    c: InternalAlignment(g38,g37)
    c: InternalAlignment(g39,g37)
    c: Weight(g40) = 1
    c: Equal(g40,g41)
    c: Equal(g40,g42)
    c: InternalAlignment(g40,g43)
    c: InternalAlignment(g41,g43)
    c: InternalAlignment(g42,g43)
    c: InternalAlignment(g44,g43)
    c: InternalAlignment(g45,g43)
    c: Block(g37)
    c: Block(g43)
    c: Coincident(g46,g4)
    c: Coincident(g46,g3)
    c: Horizontal(g46)
    c: Distance(g46) = 450
    c: Coincident(g47,g4)
    c: Coincident(g47,g3)
    c: Horizontal(g47)
    c: Horizontal(g48)
    c: Coincident(g2,g48)
    c: Block(g48)
    c: Coincident(g1,g48)
    c: Weight(g49) = 1
    c: Equal(g49,g50)
    c: Equal(g49,g51)
    c: InternalAlignment(g49,g52)
    c: InternalAlignment(g50,g52)
    c: InternalAlignment(g51,g52)
    c: InternalAlignment(g53,g52)
    c: InternalAlignment(g54,g52)
    c: Block(g52)
    c: Weight(g55) = 1
    c: Equal(g55,g56)
    c: Equal(g55,g57)
    c: InternalAlignment(g55,g58)
    c: InternalAlignment(g56,g58)
    c: InternalAlignment(g57,g58)
    c: InternalAlignment(g59,g58)
    c: InternalAlignment(g60,g58)
    c: Block(g58)
    c: Weight(g61) = 1
    c: Equal(g61,g62)
    c: Equal(g61,g63)
    c: InternalAlignment(g61,g64)
    c: InternalAlignment(g62,g64)
    c: InternalAlignment(g63,g64)
    c: InternalAlignment(g65,g64)
    c: InternalAlignment(g66,g64)
    c: Block(g64)
    c: Weight(g67) = 1
    c: Equal(g67,g68)
    c: Equal(g67,g69)
    c: InternalAlignment(g67,g70)
    c: InternalAlignment(g68,g70)
    c: InternalAlignment(g69,g70)
    c: InternalAlignment(g71,g70)
    c: InternalAlignment(g72,g70)
    c: Block(g70)
    c: Weight(g73) = 1
    c: Equal(g73,g74)
    c: Equal(g73,g75)
    c: InternalAlignment(g73,g76)
    c: InternalAlignment(g74,g76)
    c: InternalAlignment(g75,g76)
    c: InternalAlignment(g77,g76)
    c: InternalAlignment(g78,g76)
    c: Weight(g79) = 1
    c: Equal(g79,g80)
    c: Equal(g79,g81)
    c: InternalAlignment(g79,g82)
    c: InternalAlignment(g80,g82)
    c: InternalAlignment(g81,g82)
    c: InternalAlignment(g83,g82)
    c: InternalAlignment(g84,g82)
    c: Block(g76)
    c: Block(g82)
    c: Coincident(g85,g76)
    c: Coincident(g85,g82)
    c: Vertical(g85)
    c: Coincident(g86,g76)
    c: Coincident(g86,g58)
    c: Coincident(g87,g58)
    c: Coincident(g87,g82)
    c: Weight(g88) = 1
    c: Equal(g88,g89)
    c: Equal(g88,g90)
    c: InternalAlignment(g88,g91)
    c: InternalAlignment(g89,g91)
    c: InternalAlignment(g90,g91)
    c: InternalAlignment(g92,g91)
    c: InternalAlignment(g93,g91)
    c: Weight(g94) = 1
    c: Equal(g94,g95)
    c: Equal(g94,g96)
    c: InternalAlignment(g94,g97)
    c: InternalAlignment(g95,g97)
    c: InternalAlignment(g96,g97)
    c: InternalAlignment(g98,g97)
    c: InternalAlignment(g99,g97)
    c: Block(g91)
    c: Block(g97)
    c: Coincident(g100,g91)
    c: Coincident(g100,g97)
    c: Vertical(g100)
    c: Coincident(g101,g91)
    c: Coincident(g101,g52)
    c: Coincident(g102,g52)
    c: Coincident(g102,g97)
    c: Weight(g103) = 1
    c: Equal(g103,g104)
    c: Equal(g103,g105)
    c: InternalAlignment(g103,g106)
    c: InternalAlignment(g104,g106)
    c: InternalAlignment(g105,g106)
    c: InternalAlignment(g107,g106)
    c: InternalAlignment(g108,g106)
    c: Weight(g109) = 1
    c: Equal(g109,g110)
    c: Equal(g109,g111)
    c: InternalAlignment(g109,g112)
    c: InternalAlignment(g110,g112)
    c: InternalAlignment(g111,g112)
    c: InternalAlignment(g113,g112)
    c: InternalAlignment(g114,g112)
    c: Block(g106)
    c: Block(g112)
    c: Coincident(g115,g106)
    c: Coincident(g115,g112)
    c: Vertical(g115)
    c: Coincident(g116,g112)
    c: Coincident(g116,g70)
    c: Coincident(g117,g70)
    c: Coincident(g117,g106)
    c: Weight(g118) = 1
    c: Equal(g118,g119)
    c: Equal(g118,g120)
    c: InternalAlignment(g118,g121)
    c: InternalAlignment(g119,g121)
    c: InternalAlignment(g120,g121)
    c: InternalAlignment(g122,g121)
    c: InternalAlignment(g123,g121)
    c: Weight(g124) = 1
    c: Equal(g124,g125)
    c: Equal(g124,g126)
    c: InternalAlignment(g124,g127)
    c: InternalAlignment(g125,g127)
    c: InternalAlignment(g126,g127)
    c: InternalAlignment(g128,g127)
    c: InternalAlignment(g129,g127)
    c: Block(g121)
    c: Block(g127)
    c: Coincident(g130,g121)
    c: Coincident(g130,g127)
    c: Vertical(g130)
    c: Coincident(g131,g127)
    c: Coincident(g131,g64)
    c: Coincident(g132,g64)
    c: Coincident(g132,g121)
    c: Weight(g133) = 1
    c: Equal(g133,g134)
    c: Equal(g133,g135)
    c: InternalAlignment(g133,g136)
    c: InternalAlignment(g134,g136)
    c: InternalAlignment(g135,g136)
    c: InternalAlignment(g137,g136)
    c: InternalAlignment(g138,g136)
    c: Weight(g139) = 1
    c: Equal(g139,g140)
    c: Equal(g139,g141)
    c: InternalAlignment(g139,g142)
    c: InternalAlignment(g140,g142)
    c: InternalAlignment(g141,g142)
    c: InternalAlignment(g143,g142)
    c: InternalAlignment(g144,g142)
    c: Weight(g145) = 1
    c: Equal(g145,g146)
    c: Equal(g145,g147)
    c: InternalAlignment(g145,g148)
    c: InternalAlignment(g146,g148)
    c: InternalAlignment(g147,g148)
    c: InternalAlignment(g149,g148)
    c: InternalAlignment(g150,g148)
    c: Weight(g151) = 1
    c: Equal(g151,g152)
    c: Equal(g151,g153)
    c: InternalAlignment(g151,g154)
    c: InternalAlignment(g152,g154)
    c: InternalAlignment(g153,g154)
    c: InternalAlignment(g155,g154)
    c: InternalAlignment(g156,g154)
    c: Block(g154)
    c: Block(g148)
    c: Block(g142)
    c: Block(g136)
    c: Coincident(g157,g31)
    c: Coincident(g157,g154)
    c: Coincident(g158,g154)
    c: Coincident(g158,g148)
    c: Horizontal(g158)
    c: Coincident(g159,g148)
    c: Coincident(g159,g31)
    c: Vertical(g159)
    c: Coincident(g160,g25)
    c: Coincident(g160,g142)
    c: Vertical(g160)
    c: Coincident(g161,g142)
    c: Coincident(g161,g136)
    c: Horizontal(g161)
    c: Coincident(g162,g136)
    c: Coincident(g162,g25)
    c: Weight(g163) = 1
    c: Equal(g163,g164)
    c: Equal(g163,g165)
    c: InternalAlignment(g163,g166)
    c: InternalAlignment(g164,g166)
    c: InternalAlignment(g165,g166)
    c: InternalAlignment(g167,g166)
    c: InternalAlignment(g168,g166)
    c: Weight(g169) = 1
    c: Equal(g169,g170)
    c: Equal(g169,g171)
    c: InternalAlignment(g169,g172)
    c: InternalAlignment(g170,g172)
    c: InternalAlignment(g171,g172)
    c: InternalAlignment(g173,g172)
    c: InternalAlignment(g174,g172)
    c: Weight(g175) = 1
    c: Equal(g175,g176)
    c: Equal(g175,g177)
    c: InternalAlignment(g175,g178)
    c: InternalAlignment(g176,g178)
    c: InternalAlignment(g177,g178)
    c: InternalAlignment(g179,g178)
    c: InternalAlignment(g180,g178)
    c: Weight(g181) = 1
    c: Equal(g181,g182)
    c: Equal(g181,g183)
    c: InternalAlignment(g181,g184)
    c: InternalAlignment(g182,g184)
    c: InternalAlignment(g183,g184)
    c: InternalAlignment(g185,g184)
    c: InternalAlignment(g186,g184)
    c: Block(g184)
    c: Block(g178)
    c: Block(g172)
    c: Block(g166)
    c: Coincident(g187,g184)
    c: Coincident(g187,g178)
    c: Horizontal(g187)
    c: Coincident(g188,g178)
    c: Coincident(g188,g13)
    c: Vertical(g188)
    c: Coincident(g189,g19)
    c: Coincident(g189,g172)
    c: Vertical(g189)
    c: Coincident(g190,g172)
    c: Coincident(g190,g166)
    c: Horizontal(g190)
    c: Coincident(g191,g166)
    c: Coincident(g191,g19)
    c: Coincident(g192,g13)
    c: Weight(g193) = 1
    c: Equal(g193,g194)
    c: Equal(g193,g195)
    c: InternalAlignment(g193,g196)
    c: InternalAlignment(g194,g196)
    c: InternalAlignment(g195,g196)
    c: InternalAlignment(g197,g196)
    c: InternalAlignment(g198,g196)
    c: Weight(g199) = 1
    c: Equal(g199,g200)
    c: Equal(g199,g201)
    c: InternalAlignment(g199,g202)
    c: InternalAlignment(g200,g202)
    c: InternalAlignment(g201,g202)
    c: InternalAlignment(g203,g202)
    c: InternalAlignment(g204,g202)
    c: Block(g202)
    c: Block(g196)
    c: Coincident(g205,g202)
    c: Coincident(g205,g37)
    c: Coincident(g206,g37)
    c: Coincident(g206,g196)
    c: Coincident(g207,g196)
    c: Coincident(g207,g202)
    c: Vertical(g207)
    c: Weight(g208) = 1
    c: Equal(g208,g209)
    c: Equal(g208,g210)
    c: InternalAlignment(g208,g211)
    c: InternalAlignment(g209,g211)
    c: InternalAlignment(g210,g211)
    c: InternalAlignment(g212,g211)
    c: InternalAlignment(g213,g211)
    c: Weight(g214) = 1
    c: Equal(g214,g215)
    c: Equal(g214,g216)
    c: InternalAlignment(g214,g217)
    c: InternalAlignment(g215,g217)
    c: InternalAlignment(g216,g217)
    c: InternalAlignment(g218,g217)
    c: InternalAlignment(g219,g217)
    c: Block(g217)
    c: Block(g211)
    c: Coincident(g220,g211)
    c: Coincident(g220,g43)
    c: Coincident(g221,g43)
    c: Coincident(g221,g217)
    c: Coincident(g222,g217)
    c: Coincident(g222,g211)
    c: Vertical(g222)
    c: Horizontal(g223)
    c: Block(g223)
    c: Vertical(g224)
    c: Block(g224)
    c: Block(g225)
    c: Weight(g226) = 1
    c: Equal(g226,g227)
    c: Equal(g226,g228)
    c: InternalAlignment(g226,g229)
    c: InternalAlignment(g227,g229)
    c: InternalAlignment(g228,g229)
    c: InternalAlignment(g230,g229)
    c: InternalAlignment(g231,g229)
    c: Weight(g232) = 1
    c: Equal(g232,g233)
    c: Equal(g232,g234)
    c: InternalAlignment(g232,g235)
    c: InternalAlignment(g233,g235)
    c: InternalAlignment(g234,g235)
    c: InternalAlignment(g236,g235)
    c: InternalAlignment(g237,g235)
    c: Weight(g238) = 1
    c: Equal(g238,g239)
    c: Equal(g238,g240)
    c: InternalAlignment(g238,g241)
    c: InternalAlignment(g239,g241)
    c: InternalAlignment(g240,g241)
    c: InternalAlignment(g242,g241)
    c: InternalAlignment(g243,g241)
    c: Weight(g244) = 1
    c: Equal(g244,g245)
    c: Equal(g244,g246)
    c: InternalAlignment(g244,g247)
    c: InternalAlignment(g245,g247)
    c: InternalAlignment(g246,g247)
    c: InternalAlignment(g248,g247)
    c: InternalAlignment(g249,g247)
    c: Block(g229)
    c: Block(g235)
    c: Block(g241)
    c: Block(g247)
    c: Coincident(g250,g235)
    c: Coincident(g250,g229)
    c: Horizontal(g250)
    c: Block(g192)
    c: Weight(g251) = 1
    c: Equal(g251,g252)
    c: Equal(g251,g253)
    c: InternalAlignment(g251,g254)
    c: InternalAlignment(g252,g254)
    c: InternalAlignment(g253,g254)
    c: InternalAlignment(g255,g254)
    c: InternalAlignment(g256,g254)
    c: Weight(g257) = 1
    c: Equal(g257,g258)
    c: Equal(g257,g259)
    c: InternalAlignment(g257,g260)
    c: InternalAlignment(g258,g260)
    c: InternalAlignment(g259,g260)
    c: InternalAlignment(g261,g260)
    c: InternalAlignment(g262,g260)
    c: Block(g254)
    c: Block(g260)
    c: Coincident(g263,g254)
    c: Coincident(g263,g260)
    c: Weight(g264) = 1
    c: Equal(g264,g265)
    c: Equal(g264,g266)
    c: InternalAlignment(g264,g267)
    c: InternalAlignment(g265,g267)
    c: InternalAlignment(g266,g267)
    c: InternalAlignment(g268,g267)
    c: InternalAlignment(g269,g267)
    c: Weight(g270) = 1
    c: Equal(g270,g271)
    c: Equal(g270,g272)
    c: InternalAlignment(g270,g273)
    c: InternalAlignment(g271,g273)
    c: InternalAlignment(g272,g273)
    c: InternalAlignment(g274,g273)
    c: InternalAlignment(g275,g273)
    c: Weight(g276) = 1
    c: Equal(g276,g277)
    c: Equal(g276,g278)
    c: InternalAlignment(g276,g279)
    c: InternalAlignment(g277,g279)
    c: InternalAlignment(g278,g279)
    c: InternalAlignment(g280,g279)
    c: InternalAlignment(g281,g279)
    c: Block(g279)
    c: Block(g273)
    c: Block(g267)
    c: Coincident(g282,g273)
    c: Coincident(g282,g267)
    c: Coincident(g283,g267)
    c: Coincident(g283,g279)
    c: Vertical(g283)
    c: Coincident(g284,g279)
    c: Coincident(g284,g273)
    c: Horizontal(g284)
    c: Weight(g285) = 1
    c: Equal(g285,g286)
    c: InternalAlignment(g285,g287)
    c: InternalAlignment(g286,g287)
    c: InternalAlignment(g288,g287)
    c: InternalAlignment(g289,g287)
    c: Weight(g290) = 1
    c: InternalAlignment(g291,g293)
    c: InternalAlignment(g292,g293)
    c: InternalAlignment(g294,g293)
    c: InternalAlignment(g295,g293)
    c: Weight(g296) = 1
    c: Equal(g296,g297)
    c: Equal(g296,g298)
    c: InternalAlignment(g296,g299)
    c: InternalAlignment(g297,g299)
    c: InternalAlignment(g298,g299)
    c: InternalAlignment(g300,g299)
    c: InternalAlignment(g301,g299)
    c: Equal(g302,g303)
    c: Equal(g302,g304)
    c: InternalAlignment(g302,g305)
    c: InternalAlignment(g303,g305)
    c: InternalAlignment(g304,g305)
    c: InternalAlignment(g306,g305)
    c: InternalAlignment(g307,g305)
    c: Block(g293)
    c: Block(g299)
    c: Block(g305)
    c: Block(g287)
    c: Coincident(g308,g287)
    c: Coincident(g308,g293)
    c: Horizontal(g308)
    c: Coincident(g309,g293)
    c: Coincident(g309,g299)
    c: Vertical(g309)
    c: Coincident(g310,g299)
    c: Coincident(g310,g305)
    c: Horizontal(g310)
    c: Coincident(g311,g305)
    c: Coincident(g311,g287)
    c: Weight(g312) = 1
    c: Equal(g312,g313)
    c: Equal(g312,g314)
    c: InternalAlignment(g312,g315)
    c: InternalAlignment(g313,g315)
    c: InternalAlignment(g314,g315)
    c: InternalAlignment(g316,g315)
    c: InternalAlignment(g317,g315)
    c: Weight(g318) = 1
    c: Equal(g318,g319)
    c: Equal(g318,g320)
    c: InternalAlignment(g318,g321)
    c: InternalAlignment(g319,g321)
    c: InternalAlignment(g320,g321)
    c: InternalAlignment(g322,g321)
    c: InternalAlignment(g323,g321)
    c: Weight(g324) = 1
    c: Equal(g324,g325)
    c: Equal(g324,g326)
    c: InternalAlignment(g324,g327)
    c: InternalAlignment(g325,g327)
    c: InternalAlignment(g326,g327)
    c: InternalAlignment(g328,g327)
    c: InternalAlignment(g329,g327)
    c: Block(g327)
    c: Block(g321)
    c: Block(g315)
    c: Coincident(g330,g327)
    c: Coincident(g330,g321)
    c: Horizontal(g330)
    c: Coincident(g331,g321)
    c: Coincident(g331,g315)
    c: Vertical(g331)
    c: Coincident(g332,g315)
    c: Coincident(g332,g327)
    c: InternalAlignment(g333,g334)
    c: InternalAlignment(g335,g334)
    c: InternalAlignment(g336,g334)
    c: Block(g334)
    c: Equal(g337,g338)
    c: Equal(g337,g339)
    c: InternalAlignment(g337,g340)
    c: InternalAlignment(g338,g340)
    c: InternalAlignment(g339,g340)
    c: InternalAlignment(g341,g340)
    c: InternalAlignment(g342,g340)
    c: Block(g340)
    c: Coincident(g343,g334)
    c: Horizontal(g343)
    c: Block(g343)
    c: Coincident(g344,g334)
    c: Coincident(g344,g260)
    c: Vertical(g344)
    c: Coincident(g345,g340)
    c: Coincident(g345,g254)
    c: Vertical(g345)
    c: Coincident(g347,g5)
    c: Coincident(g348,g5)
    c: Block(g346)
    c: Block(g5)
    c: Block(g348)
    c: Block(g347)
    c: Distance(g344) = 119.89
FEATURE [Sketcher::SketchObject] Sketch001
  FullyConstrained = true
  MapMode = 4
  Placement = pos=(0,0,0) rot=(0.57735,0.57735,0.57735;2.0944rad)
  Support = -> [Sketch]
  sketch-geometry (46):
    g0: BSplineCurve PolesCount=3 KnotsCount=2 Degree=2 IsPeriodic=0
    g1: ArcOfCircle CenterX=73.1223 CenterY=-32.291 CenterZ=0 NormalX=0 NormalY=0 NormalZ=1 AngleXU=0 Radius=13 StartAngle=5.92268 EndAngle=9.06428
    g2: ArcOfCircle CenterX=66.7816 CenterY=-49.1439 CenterZ=0 NormalX=0 NormalY=0 NormalZ=1 AngleXU=0 Radius=13 StartAngle=2.78068 EndAngle=5.92131
    g3: ArcOfCircle CenterX=55.9263 CenterY=-78.1807 CenterZ=0 NormalX=0 NormalY=0 NormalZ=1 AngleXU=0 Radius=13 StartAngle=5.92268 EndAngle=9.06428
    g4: ArcOfCircle CenterX=49.5884 CenterY=-95.0342 CenterZ=0 NormalX=0 NormalY=0 NormalZ=1 AngleXU=0 Radius=13 StartAngle=2.78068 EndAngle=5.92131
    g5: ArcOfCircle CenterX=38.7206 CenterY=-124.067 CenterZ=0 NormalX=0 NormalY=0 NormalZ=1 AngleXU=0 Radius=13 StartAngle=5.92268 EndAngle=9.06428
    g6: ArcOfCircle CenterX=32.3875 CenterY=-140.92 CenterZ=0 NormalX=0 NormalY=0 NormalZ=1 AngleXU=0 Radius=13 StartAngle=2.78068 EndAngle=5.92131
    g7: ArcOfCircle CenterX=21.4715 CenterY=-169.934 CenterZ=0 NormalX=0 NormalY=0 NormalZ=1 AngleXU=0 Radius=13 StartAngle=5.92268 EndAngle=9.06428
    g8: ArcOfCircle CenterX=15.1336 CenterY=-186.787 CenterZ=0 NormalX=0 NormalY=0 NormalZ=1 AngleXU=0 Radius=13 StartAngle=2.78068 EndAngle=5.92131
    g9-g12: Circle x4 (B-spline internal-alignment scaffolding for g13; pole/knot coordinates omitted)
    g13: BSplineCurve PolesCount=4 KnotsCount=2 Degree=3 IsPeriodic=0
    g14: GeomPoint X=28.8094 Y=-19.0875 Z=0
    g15: GeomPoint X=47.0443 Y=-50.4712 Z=0
    g16: Circle CenterX=53.5586 CenterY=-23.2695 CenterZ=0 NormalX=0 NormalY=0 NormalZ=1 AngleXU=0 Radius=3.24518
    g17: Circle CenterX=-195.441 CenterY=-127.082 CenterZ=0 NormalX=0 NormalY=0 NormalZ=1 AngleXU=0 Radius=1
    g18: Circle CenterX=-8.24091 CenterY=-197.481 CenterZ=0 NormalX=0 NormalY=0 NormalZ=1 AngleXU=0 Radius=1
    g19: Circle CenterX=12.8789 CenterY=-141.321 CenterZ=0 NormalX=0 NormalY=0 NormalZ=1 AngleXU=0 Radius=1
    g20: BSplineCurve PolesCount=3 KnotsCount=2 Degree=2 IsPeriodic=0
    g21: GeomPoint X=-195.441 Y=-127.082 Z=0
    g22: GeomPoint X=12.8789 Y=-141.321 Z=0
    g23: Circle CenterX=-12.8016 CenterY=-179.036 CenterZ=0 NormalX=0 NormalY=0 NormalZ=1 AngleXU=0 Radius=10.5072
    g24: Circle CenterX=0.933922 CenterY=-166.43 CenterZ=0 NormalX=0 NormalY=0 NormalZ=1 AngleXU=0 Radius=3.26661
    g25: Circle CenterX=-33.5518 CenterY=-176.44 CenterZ=0 NormalX=0 NormalY=0 NormalZ=1 AngleXU=0 Radius=5.64388
    g26: Circle CenterX=-47.2366 CenterY=-173.859 CenterZ=0 NormalX=0 NormalY=0 NormalZ=1 AngleXU=0 Radius=3.01653
    g27: Circle CenterX=-56.2595 CenterY=-171.456 CenterZ=0 NormalX=0 NormalY=0 NormalZ=1 AngleXU=0 Radius=2.12826
    g28: ArcOfCircle CenterX=51.2151 CenterY=-198.473 CenterZ=0 NormalX=0 NormalY=0 NormalZ=1 AngleXU=0 Radius=20 StartAngle=2.78189 EndAngle=4.35269
    g29: LineSegment StartX=32.4951 StartY=-191.433 StartZ=0 EndX=94.6578 EndY=-26.1352 EndZ=0
    g30: LineSegment StartX=43.1192 StartY=-220.001 StartZ=0 EndX=-196.497 EndY=-129.89 EndZ=0
    g31: LineSegment StartX=43.1192 StartY=-220.001 StartZ=0 EndX=44.1752 EndY=-217.193 EndZ=0
    g32: LineSegment StartX=117.223 StartY=-19.0875 StartZ=0 EndX=117.223 EndY=-16.0875 EndZ=0
    g33: LineSegment StartX=117.223 StartY=-16.0875 StartZ=0 EndX=17.2232 EndY=-16.0875 EndZ=0
    g34: LineSegment StartX=17.2232 StartY=-16.0875 StartZ=0 EndX=17.2232 EndY=-19.0875 EndZ=0
    g35: LineSegment StartX=28.8094 StartY=-19.0875 StartZ=0 EndX=17.2232 EndY=-19.0875 EndZ=0
    g36: LineSegment StartX=47.0443 StartY=-50.4712 StartZ=0 EndX=12.8789 EndY=-141.321 EndZ=0
    g37: LineSegment StartX=-195.441 StartY=-127.082 StartZ=0 EndX=-196.497 EndY=-129.89 EndZ=0
    g38: LineSegment StartX=85.2866 StartY=-36.8766 StartZ=0 EndX=78.9396 EndY=-53.7463 EndZ=0
    g39: LineSegment StartX=60.9579 StartY=-27.7053 StartZ=0 EndX=54.6191 EndY=-44.5532 EndZ=0
    g40: LineSegment StartX=68.0907 StartY=-82.7664 StartZ=0 EndX=61.7465 EndY=-99.6365 EndZ=0
    g41: LineSegment StartX=43.7619 StartY=-73.595 StartZ=0 EndX=37.426 EndY=-90.4435 EndZ=0
    g42: LineSegment StartX=50.885 StartY=-128.652 StartZ=0 EndX=44.5456 EndY=-145.522 EndZ=0
    g43: LineSegment StartX=26.5562 StartY=-119.481 StartZ=0 EndX=20.2251 EndY=-136.329 EndZ=0
    g44: LineSegment StartX=9.3071 StartY=-165.349 StartZ=0 EndX=2.97115 EndY=-182.197 EndZ=0
    g45: LineSegment StartX=33.6358 StartY=-174.52 StartZ=0 EndX=27.2917 EndY=-191.39 EndZ=0
  constraints (71):
    c: Block(g0)
    c: Block(g1)
    c: Block(g2)
    c: Block(g4)
    c: Block(g3)
    c: Block(g6)
    c: Block(g5)
    c: Block(g8)
    c: Block(g7)
    c: Weight(g9) = 1
    c: Equal(g9,g10)
    c: Equal(g9,g11)
    c: Equal(g9,g12)
    c: InternalAlignment(g9-g12 -> g13) x4
    c: InternalAlignment(g14,g13)
    c: InternalAlignment(g15,g13)
    c: Block(g16)
    c: Weight(g17) = 1
    c: Equal(g17,g18)
    c: Equal(g17,g19)
    c: InternalAlignment(g17,g20)
    c: InternalAlignment(g18,g20)
    c: InternalAlignment(g19,g20)
    c: InternalAlignment(g21,g20)
    c: InternalAlignment(g22,g20)
    c: Block(g20)
    c: Block(g23)
    c: Block(g24)
    c: Block(g25)
    c: Block(g26)
    c: Block(g27)
    c: Block(g28)
    c: Coincident(g29,g28)
    c: Coincident(g29,g0)
    c: Block(g13)
    c: Coincident(g31,g30)
    c: Coincident(g31,g28)
    c: Block(g31)
    c: Coincident(g32,g0)
    c: Vertical(g32)
    c: Coincident(g33,g32)
    c: Horizontal(g33)
    c: Coincident(g34,g33)
    c: Vertical(g34)
    c: Block(g33)
    c: Coincident(g35,g13)
    c: Coincident(g35,g34)
    c: Horizontal(g35)
    c: Coincident(g36,g13)
    c: Coincident(g36,g20)
    c: Coincident(g37,g20)
    c: Coincident(g37,g30)
    c: Block(g30)
    c: Coincident(g38,g1)
    c: Coincident(g38,g2)
    c: Coincident(g39,g1)
    c: Coincident(g39,g2)
    c: Coincident(g40,g3)
    c: Coincident(g40,g4)
    c: Coincident(g41,g3)
    c: Coincident(g41,g4)
    c: Coincident(g42,g5)
    c: Coincident(g42,g6)
    c: Coincident(g43,g5)
    c: Coincident(g43,g6)
    c: Coincident(g44,g7)
    c: Coincident(g44,g8)
    c: Coincident(g45,g7)
    c: Coincident(g45,g8)
    c: Distance(g30) = 256
    c: Distance(g33) = 100
FEATURE [Part::Extrusion] Extrude002
  Base = -> Sketch001
  Dir = (1,0,0)
  DirMode = 2
  FaceMakerClass = Part::FaceMakerBullseye
  LengthFwd = 8
  LengthRev = 0
  Solid = true
  Symmetric = false
FEATURE [Sketcher::SketchObject] Sketch002
  FullyConstrained = true
  sketch-geometry (20):
    g0: LineSegment StartX=-2.77179 StartY=-200.304 StartZ=0 EndX=5.22821 EndY=-200.304 EndZ=0
    g1: LineSegment StartX=5.22821 StartY=-200.304 StartZ=0 EndX=5.22821 EndY=-197.304 EndZ=0
    g2: LineSegment StartX=-2.77179 StartY=-200.304 StartZ=0 EndX=-2.77179 EndY=-197.304 EndZ=0
    g3: LineSegment StartX=5.22821 StartY=-197.304 StartZ=0 EndX=8.22821 EndY=-197.304 EndZ=0
    g4: LineSegment StartX=-2.77179 StartY=-197.304 StartZ=0 EndX=-5.77179 EndY=-197.304 EndZ=0
    g5: LineSegment StartX=19.2282 StartY=-203.304 StartZ=0 EndX=19.2282 EndY=-206.304 EndZ=0
    g6: LineSegment StartX=-16.7718 StartY=-203.304 StartZ=0 EndX=-16.7718 EndY=-206.304 EndZ=0
    g7: LineSegment StartX=-16.7718 StartY=-206.304 StartZ=0 EndX=19.2282 EndY=-206.304 EndZ=0
    g8: Circle CenterX=-16.7718 CenterY=-203.304 CenterZ=0 NormalX=0 NormalY=0 NormalZ=1 AngleXU=0 Radius=1
    g9: Circle CenterX=-5.77179 CenterY=-203.304 CenterZ=0 NormalX=0 NormalY=0 NormalZ=1 AngleXU=0 Radius=1
    g10: Circle CenterX=-5.77179 CenterY=-197.304 CenterZ=0 NormalX=0 NormalY=0 NormalZ=1 AngleXU=0 Radius=1
    g11: BSplineCurve PolesCount=3 KnotsCount=2 Degree=2 IsPeriodic=0
    g12: GeomPoint X=-16.7718 Y=-203.304 Z=0
    g13: GeomPoint X=-5.77179 Y=-197.304 Z=0
    g14: Circle CenterX=19.2282 CenterY=-203.304 CenterZ=0 NormalX=0 NormalY=0 NormalZ=1 AngleXU=0 Radius=1
    g15: Circle CenterX=8.22821 CenterY=-203.304 CenterZ=0 NormalX=0 NormalY=0 NormalZ=1 AngleXU=0 Radius=1
    g16: Circle CenterX=8.22821 CenterY=-197.304 CenterZ=0 NormalX=0 NormalY=0 NormalZ=1 AngleXU=0 Radius=1
    g17: BSplineCurve PolesCount=3 KnotsCount=2 Degree=2 IsPeriodic=0
    g18: GeomPoint X=19.2282 Y=-203.304 Z=0
    g19: GeomPoint X=8.22821 Y=-197.304 Z=0
  constraints (41):
    c: Horizontal(g0)
    c: Distance(g0) = 8
    c: Coincident(g1,g0)
    c: Vertical(g1)
    c: Distance(g1) = 3
    c: Coincident(g2,g0)
    c: Vertical(g2)
    c: Distance(g2) = 3
    c: Coincident(g3,g1)
    c: Horizontal(g3)
    c: Distance(g3) = 3
    c: Coincident(g4,g2)
    c: Horizontal(g4)
    c: Distance(g4) = 3
    c: Vertical(g5)
    c: Vertical(g6)
    c: Coincident(g7,g6)
    c: Coincident(g7,g5)
    c: Weight(g8) = 1
    c: Equal(g8,g9)
    c: Equal(g8,g10)
    c: Coincident(g11,g4)
    c: InternalAlignment(g8,g11)
    c: InternalAlignment(g9,g11)
    c: InternalAlignment(g10,g11)
    c: InternalAlignment(g12,g11)
    c: InternalAlignment(g13,g11)
    c: Coincident(g17,g5)
    c: Weight(g14) = 1
    c: Equal(g14,g15)
    c: Equal(g14,g16)
    c: Coincident(g17,g3)
    c: InternalAlignment(g14,g17)
    c: InternalAlignment(g15,g17)
    c: InternalAlignment(g16,g17)
    c: InternalAlignment(g18,g17)
    c: InternalAlignment(g19,g17)
    c: Block(g7)
    c: Block(g17)
    c: Block(g11)
    c: Block(g6)
FEATURE [Part::Extrusion] Extrude003
  Base = -> Sketch002
  Dir = (0,0,1)
  DirMode = 2
  FaceMakerClass = Part::FaceMakerBullseye
  LengthFwd = 260
  LengthRev = 0
  Solid = true
  Symmetric = false
FEATURE [Sketcher::SketchObject] Sketch003
  FullyConstrained = false
  sketch-geometry (421):
    g0: LineSegment StartX=-42.9272 StartY=136.221 StartZ=0 EndX=-42.9272 EndY=-103.779 EndZ=0
    g1: LineSegment StartX=407.073 StartY=136.221 StartZ=0 EndX=407.073 EndY=-103.779 EndZ=0
    g2: ArcOfCircle CenterX=-26.9272 CenterY=-83.7794 CenterZ=0 NormalX=0 NormalY=0 NormalZ=1 AngleXU=0 Radius=8 StartAngle=3.14159 EndAngle=6.28319
    g3: ArcOfCircle CenterX=391.073 CenterY=-83.7794 CenterZ=0 NormalX=0 NormalY=0 NormalZ=1 AngleXU=0 Radius=8 StartAngle=3.14159 EndAngle=6.28319
    g4: Circle CenterX=175.022 CenterY=27.0628 CenterZ=0 NormalX=0 NormalY=0 NormalZ=1 AngleXU=0 Radius=1
    g5: Circle CenterX=179.022 CenterY=24.8665 CenterZ=0 NormalX=0 NormalY=0 NormalZ=1 AngleXU=0 Radius=1
    g6: Circle CenterX=179.022 CenterY=27.0628 CenterZ=0 NormalX=0 NormalY=0 NormalZ=1 AngleXU=0 Radius=1
    g7: BSplineCurve PolesCount=3 KnotsCount=2 Degree=2 IsPeriodic=0
    g8: GeomPoint X=175.022 Y=27.0628 Z=0
    g9: GeomPoint X=179.022 Y=27.0628 Z=0
    g10: Circle CenterX=189.124 CenterY=27.0628 CenterZ=0 NormalX=0 NormalY=0 NormalZ=1 AngleXU=0 Radius=1
    g11: Circle CenterX=185.124 CenterY=24.8665 CenterZ=0 NormalX=0 NormalY=0 NormalZ=1 AngleXU=0 Radius=1
    g12: Circle CenterX=185.124 CenterY=27.0628 CenterZ=0 NormalX=0 NormalY=0 NormalZ=1 AngleXU=0 Radius=1
    g13: BSplineCurve PolesCount=3 KnotsCount=2 Degree=2 IsPeriodic=0
    g14: GeomPoint X=189.124 Y=27.0628 Z=0
    g15: GeomPoint X=185.124 Y=27.0628 Z=0
    g16: Circle CenterX=175.022 CenterY=5.37834 CenterZ=0 NormalX=0 NormalY=0 NormalZ=1 AngleXU=0 Radius=1
    g17: Circle CenterX=179.022 CenterY=7.57463 CenterZ=0 NormalX=0 NormalY=0 NormalZ=1 AngleXU=0 Radius=1
    g18: Circle CenterX=179.022 CenterY=5.34704 CenterZ=0 NormalX=0 NormalY=0 NormalZ=1 AngleXU=0 Radius=1
    g19: BSplineCurve PolesCount=3 KnotsCount=2 Degree=2 IsPeriodic=0
    g20: GeomPoint X=175.022 Y=5.37834 Z=0
    g21: GeomPoint X=179.022 Y=5.34704 Z=0
    g22: Circle CenterX=189.124 CenterY=5.37834 CenterZ=0 NormalX=0 NormalY=0 NormalZ=1 AngleXU=0 Radius=1
    g23: Circle CenterX=185.124 CenterY=7.57463 CenterZ=0 NormalX=0 NormalY=0 NormalZ=1 AngleXU=0 Radius=1
    g24: Circle CenterX=185.124 CenterY=5.34704 CenterZ=0 NormalX=0 NormalY=0 NormalZ=1 AngleXU=0 Radius=1
    g25: BSplineCurve PolesCount=3 KnotsCount=2 Degree=2 IsPeriodic=0
    g26: GeomPoint X=189.124 Y=5.37834 Z=0
    g27: GeomPoint X=185.124 Y=5.34704 Z=0
    g28: Circle CenterX=165.871 CenterY=18.1458 CenterZ=0 NormalX=0 NormalY=0 NormalZ=1 AngleXU=0 Radius=1
    g29: Circle CenterX=169.377 CenterY=16.2206 CenterZ=0 NormalX=0 NormalY=0 NormalZ=1 AngleXU=0 Radius=1
    g30: Circle CenterX=165.871 CenterY=14.2954 CenterZ=0 NormalX=0 NormalY=0 NormalZ=1 AngleXU=0 Radius=1
    g31: BSplineCurve PolesCount=3 KnotsCount=2 Degree=2 IsPeriodic=0
    g32: GeomPoint X=165.871 Y=18.1458 Z=0
    g33: GeomPoint X=165.871 Y=14.2954 Z=0
    g34: Circle CenterX=198.275 CenterY=18.1458 CenterZ=0 NormalX=0 NormalY=0 NormalZ=1 AngleXU=0 Radius=1
    g35: Circle CenterX=194.768 CenterY=16.2206 CenterZ=0 NormalX=0 NormalY=0 NormalZ=1 AngleXU=0 Radius=1
    g36: Circle CenterX=198.275 CenterY=14.2954 CenterZ=0 NormalX=0 NormalY=0 NormalZ=1 AngleXU=0 Radius=1
    g37: BSplineCurve PolesCount=3 KnotsCount=2 Degree=2 IsPeriodic=0
    g38: GeomPoint X=198.275 Y=18.1458 Z=0
    g39: GeomPoint X=198.275 Y=14.2954 Z=0
    g40: LineSegment StartX=407.073 StartY=-103.779 StartZ=0 EndX=-42.9272 EndY=-103.779 EndZ=0
    g41: Circle CenterX=125.607 CenterY=54.1951 CenterZ=0 NormalX=0 NormalY=0 NormalZ=1 AngleXU=0 Radius=1
    g42: Circle CenterX=139.632 CenterY=46.4944 CenterZ=0 NormalX=0 NormalY=0 NormalZ=1 AngleXU=0 Radius=1
    g43: Circle CenterX=127.326 CenterY=56.7187 CenterZ=0 NormalX=0 NormalY=0 NormalZ=1 AngleXU=0 Radius=1
    g44: BSplineCurve PolesCount=3 KnotsCount=2 Degree=2 IsPeriodic=0
    g45: GeomPoint X=125.607 Y=54.1951 Z=0
    g46: GeomPoint X=127.326 Y=56.7187 Z=0
    g47: Circle CenterX=236.821 CenterY=56.7187 CenterZ=0 NormalX=0 NormalY=0 NormalZ=1 AngleXU=0 Radius=1
    g48: Circle CenterX=224.513 CenterY=46.4944 CenterZ=0 NormalX=0 NormalY=0 NormalZ=1 AngleXU=0 Radius=1
    g49: Circle CenterX=238.538 CenterY=54.1951 CenterZ=0 NormalX=0 NormalY=0 NormalZ=1 AngleXU=0 Radius=1
    g50: BSplineCurve PolesCount=3 KnotsCount=2 Degree=2 IsPeriodic=0
    g51: GeomPoint X=236.821 Y=56.7187 Z=0
    g52: GeomPoint X=238.538 Y=54.1951 Z=0
    g53: Circle CenterX=238.538 CenterY=-21.7539 CenterZ=0 NormalX=0 NormalY=0 NormalZ=1 AngleXU=0 Radius=1
    g54: Circle CenterX=224.513 CenterY=-14.0532 CenterZ=0 NormalX=0 NormalY=0 NormalZ=1 AngleXU=0 Radius=1
    g55: Circle CenterX=236.821 CenterY=-24.2775 CenterZ=0 NormalX=0 NormalY=0 NormalZ=1 AngleXU=0 Radius=1
    g56: BSplineCurve PolesCount=3 KnotsCount=2 Degree=2 IsPeriodic=0
    g57: GeomPoint X=238.538 Y=-21.7539 Z=0
    g58: GeomPoint X=236.821 Y=-24.2775 Z=0
    g59: Circle CenterX=125.607 CenterY=-21.7539 CenterZ=0 NormalX=0 NormalY=0 NormalZ=1 AngleXU=0 Radius=1
    g60: Circle CenterX=139.632 CenterY=-14.0532 CenterZ=0 NormalX=0 NormalY=0 NormalZ=1 AngleXU=0 Radius=1
    g61: Circle CenterX=127.325 CenterY=-24.2775 CenterZ=0 NormalX=0 NormalY=0 NormalZ=1 AngleXU=0 Radius=1
    g62: BSplineCurve PolesCount=3 KnotsCount=2 Degree=2 IsPeriodic=0
    g63: GeomPoint X=125.607 Y=-21.7539 Z=0
    g64: GeomPoint X=127.325 Y=-24.2775 Z=0
    g65: Circle CenterX=302.996 CenterY=111.695 CenterZ=0 NormalX=0 NormalY=0 NormalZ=1 AngleXU=0 Radius=1
    g66: Circle CenterX=306.073 CenterY=114.251 CenterZ=0 NormalX=0 NormalY=0 NormalZ=1 AngleXU=0 Radius=1
    g67: Circle CenterX=306.073 CenterY=110.251 CenterZ=0 NormalX=0 NormalY=0 NormalZ=1 AngleXU=0 Radius=1
    g68: BSplineCurve PolesCount=3 KnotsCount=2 Degree=2 IsPeriodic=0
    g69: GeomPoint X=302.996 Y=111.695 Z=0
    g70: GeomPoint X=306.073 Y=110.251 Z=0
    g71: Circle CenterX=306.073 CenterY=95.2763 CenterZ=0 NormalX=0 NormalY=0 NormalZ=1 AngleXU=0 Radius=1
    g72: Circle CenterX=306.073 CenterY=91.2763 CenterZ=0 NormalX=0 NormalY=0 NormalZ=1 AngleXU=0 Radius=1
    g73: Circle CenterX=302.567 CenterY=89.3511 CenterZ=0 NormalX=0 NormalY=0 NormalZ=1 AngleXU=0 Radius=1
    g74: BSplineCurve PolesCount=3 KnotsCount=2 Degree=2 IsPeriodic=0
    g75: GeomPoint X=306.073 Y=95.2763 Z=0
    g76: GeomPoint X=302.567 Y=89.3511 Z=0
    g77: LineSegment StartX=306.073 StartY=110.251 StartZ=0 EndX=306.073 EndY=95.2763 EndZ=0
    g78: LineSegment StartX=302.996 StartY=111.695 StartZ=0 EndX=236.821 EndY=56.7187 EndZ=0
    g79: LineSegment StartX=238.538 StartY=54.1951 StartZ=0 EndX=302.567 EndY=89.3511 EndZ=0
    g80: Circle CenterX=61.1496 CenterY=111.695 CenterZ=0 NormalX=0 NormalY=0 NormalZ=1 AngleXU=0 Radius=1
    g81: Circle CenterX=58.0728 CenterY=114.251 CenterZ=0 NormalX=0 NormalY=0 NormalZ=1 AngleXU=0 Radius=1
    g82: Circle CenterX=58.0728 CenterY=110.251 CenterZ=0 NormalX=0 NormalY=0 NormalZ=1 AngleXU=0 Radius=1
    g83: BSplineCurve PolesCount=3 KnotsCount=2 Degree=2 IsPeriodic=0
    g84: GeomPoint X=61.1496 Y=111.695 Z=0
    g85: GeomPoint X=58.0728 Y=110.251 Z=0
    g86: Circle CenterX=61.5791 CenterY=89.3511 CenterZ=0 NormalX=0 NormalY=0 NormalZ=1 AngleXU=0 Radius=1
    g87: Circle CenterX=58.0728 CenterY=91.2763 CenterZ=0 NormalX=0 NormalY=0 NormalZ=1 AngleXU=0 Radius=1
    g88: Circle CenterX=58.0728 CenterY=95.2763 CenterZ=0 NormalX=0 NormalY=0 NormalZ=1 AngleXU=0 Radius=1
    g89: BSplineCurve PolesCount=3 KnotsCount=2 Degree=2 IsPeriodic=0
    g90: GeomPoint X=61.5791 Y=89.3511 Z=0
    g91: GeomPoint X=58.0728 Y=95.2763 Z=0
    g92: LineSegment StartX=58.0728 StartY=110.251 StartZ=0 EndX=58.0728 EndY=95.2763 EndZ=0
    g93: LineSegment StartX=61.1496 StartY=111.695 StartZ=0 EndX=127.326 EndY=56.7187 EndZ=0
    g94: LineSegment StartX=125.607 StartY=54.1951 StartZ=0 EndX=61.5791 EndY=89.3511 EndZ=0
    g95: Circle CenterX=61.5791 CenterY=-56.9099 CenterZ=0 NormalX=0 NormalY=0 NormalZ=1 AngleXU=0 Radius=1
    g96: Circle CenterX=58.0728 CenterY=-58.8351 CenterZ=0 NormalX=0 NormalY=0 NormalZ=1 AngleXU=0 Radius=1
    g97: Circle CenterX=58.0728 CenterY=-62.8351 CenterZ=0 NormalX=0 NormalY=0 NormalZ=1 AngleXU=0 Radius=1
    g98: BSplineCurve PolesCount=3 KnotsCount=2 Degree=2 IsPeriodic=0
    g99: GeomPoint X=61.5791 Y=-56.9099 Z=0
    g100: GeomPoint X=58.0728 Y=-62.8351 Z=0
    g101: Circle CenterX=58.0728 CenterY=-77.8102 CenterZ=0 NormalX=0 NormalY=0 NormalZ=1 AngleXU=0 Radius=1
    g102: Circle CenterX=58.0728 CenterY=-81.8102 CenterZ=0 NormalX=0 NormalY=0 NormalZ=1 AngleXU=0 Radius=1
    g103: Circle CenterX=61.1496 CenterY=-79.2541 CenterZ=0 NormalX=0 NormalY=0 NormalZ=1 AngleXU=0 Radius=1
    g104: BSplineCurve PolesCount=3 KnotsCount=2 Degree=2 IsPeriodic=0
    g105: GeomPoint X=58.0728 Y=-77.8102 Z=0
    g106: GeomPoint X=61.1496 Y=-79.2541 Z=0
    g107: LineSegment StartX=58.0728 StartY=-62.8351 StartZ=0 EndX=58.0728 EndY=-77.8102 EndZ=0
    g108: LineSegment StartX=61.1496 StartY=-79.2541 StartZ=0 EndX=127.325 EndY=-24.2775 EndZ=0
    g109: LineSegment StartX=125.607 StartY=-21.7539 StartZ=0 EndX=61.5791 EndY=-56.9099 EndZ=0
    g110: Circle CenterX=302.567 CenterY=-56.9099 CenterZ=0 NormalX=0 NormalY=0 NormalZ=1 AngleXU=0 Radius=1
    g111: Circle CenterX=306.073 CenterY=-58.8351 CenterZ=0 NormalX=0 NormalY=0 NormalZ=1 AngleXU=0 Radius=1
    g112: Circle CenterX=306.073 CenterY=-62.8351 CenterZ=0 NormalX=0 NormalY=0 NormalZ=1 AngleXU=0 Radius=1
    g113: BSplineCurve PolesCount=3 KnotsCount=2 Degree=2 IsPeriodic=0
    g114: GeomPoint X=302.567 Y=-56.9099 Z=0
    g115: GeomPoint X=306.073 Y=-62.8351 Z=0
    g116: Circle CenterX=302.996 CenterY=-79.2541 CenterZ=0 NormalX=0 NormalY=0 NormalZ=1 AngleXU=0 Radius=1
    g117: Circle CenterX=306.073 CenterY=-81.8102 CenterZ=0 NormalX=0 NormalY=0 NormalZ=1 AngleXU=0 Radius=1
    g118: Circle CenterX=306.073 CenterY=-77.8102 CenterZ=0 NormalX=0 NormalY=0 NormalZ=1 AngleXU=0 Radius=1
    g119: BSplineCurve PolesCount=3 KnotsCount=2 Degree=2 IsPeriodic=0
    g120: GeomPoint X=302.996 Y=-79.2541 Z=0
    g121: GeomPoint X=306.073 Y=-77.8102 Z=0
    g122: LineSegment StartX=306.073 StartY=-62.8351 StartZ=0 EndX=306.073 EndY=-77.8102 EndZ=0
    g123: LineSegment StartX=302.996 StartY=-79.2541 StartZ=0 EndX=236.821 EndY=-24.2775 EndZ=0
    g124: LineSegment StartX=238.538 StartY=-21.7539 StartZ=0 EndX=302.567 EndY=-56.9099 EndZ=0
    g125: Circle CenterX=61.6457 CenterY=-88.8112 CenterZ=0 NormalX=0 NormalY=0 NormalZ=1 AngleXU=0 Radius=1
    g126: Circle CenterX=58.0728 CenterY=-91.7794 CenterZ=0 NormalX=0 NormalY=0 NormalZ=1 AngleXU=0 Radius=1
    g127: Circle CenterX=63.9135 CenterY=-91.7791 CenterZ=0 NormalX=0 NormalY=0 NormalZ=1 AngleXU=0 Radius=1
    g128: BSplineCurve PolesCount=3 KnotsCount=2 Degree=2 IsPeriodic=0
    g129: GeomPoint X=61.6457 Y=-88.8112 Z=0
    g130: GeomPoint X=63.9135 Y=-91.7791 Z=0
    g131: Circle CenterX=179.022 CenterY=-85.8163 CenterZ=0 NormalX=0 NormalY=0 NormalZ=1 AngleXU=0 Radius=1
    g132: Circle CenterX=179.022 CenterY=-91.7794 CenterZ=0 NormalX=0 NormalY=0 NormalZ=1 AngleXU=0 Radius=1
    g133: Circle CenterX=171.895 CenterY=-91.7791 CenterZ=0 NormalX=0 NormalY=0 NormalZ=1 AngleXU=0 Radius=1
    g134: BSplineCurve PolesCount=3 KnotsCount=2 Degree=2 IsPeriodic=0
    g135: GeomPoint X=179.022 Y=-85.8163 Z=0
    g136: GeomPoint X=171.895 Y=-91.7791 Z=0
    g137: Circle CenterX=185.124 CenterY=-86.2028 CenterZ=0 NormalX=0 NormalY=0 NormalZ=1 AngleXU=0 Radius=1
    g138: Circle CenterX=185.124 CenterY=-91.7794 CenterZ=0 NormalX=0 NormalY=0 NormalZ=1 AngleXU=0 Radius=1
    g139: Circle CenterX=191.747 CenterY=-91.7794 CenterZ=0 NormalX=0 NormalY=0 NormalZ=1 AngleXU=0 Radius=1
    g140: BSplineCurve PolesCount=3 KnotsCount=2 Degree=2 IsPeriodic=0
    g141: GeomPoint X=185.124 Y=-86.2028 Z=0
    g142: GeomPoint X=191.747 Y=-91.7794 Z=0
    g143: Circle CenterX=299.888 CenterY=-86.6413 CenterZ=0 NormalX=0 NormalY=0 NormalZ=1 AngleXU=0 Radius=1
    g144: Circle CenterX=306.073 CenterY=-91.7794 CenterZ=0 NormalX=0 NormalY=0 NormalZ=1 AngleXU=0 Radius=1
    g145: Circle CenterX=298.776 CenterY=-91.7794 CenterZ=0 NormalX=0 NormalY=0 NormalZ=1 AngleXU=0 Radius=1
    g146: BSplineCurve PolesCount=3 KnotsCount=2 Degree=2 IsPeriodic=0
    g147: GeomPoint X=299.888 Y=-86.6413 Z=0
    g148: GeomPoint X=298.776 Y=-91.7794 Z=0
    g149: LineSegment StartX=189.124 StartY=5.37834 StartZ=0 EndX=299.888 EndY=-86.6413 EndZ=0
    g150: LineSegment StartX=298.776 StartY=-91.7794 StartZ=0 EndX=191.747 EndY=-91.7794 EndZ=0
    g151: LineSegment StartX=185.124 StartY=-86.2028 StartZ=0 EndX=185.124 EndY=5.34704 EndZ=0
    g152: LineSegment StartX=179.022 StartY=5.34704 StartZ=0 EndX=179.022 EndY=-85.8163 EndZ=0
    g153: LineSegment StartX=171.895 StartY=-91.7791 StartZ=0 EndX=63.9135 EndY=-91.7791 EndZ=0
    g154: LineSegment StartX=61.6457 StartY=-88.8112 StartZ=0 EndX=175.022 EndY=5.37834 EndZ=0
    g155: Circle CenterX=302.073 CenterY=124.221 CenterZ=0 NormalX=0 NormalY=0 NormalZ=1 AngleXU=0 Radius=1
    g156: Circle CenterX=306.073 CenterY=124.221 CenterZ=0 NormalX=0 NormalY=0 NormalZ=1 AngleXU=0 Radius=1
    g157: Circle CenterX=302.996 CenterY=121.665 CenterZ=0 NormalX=0 NormalY=0 NormalZ=1 AngleXU=0 Radius=1
    g158: BSplineCurve PolesCount=3 KnotsCount=2 Degree=2 IsPeriodic=0
    g159: GeomPoint X=302.073 Y=124.221 Z=0
    g160: GeomPoint X=302.996 Y=121.665 Z=0
    g161: Circle CenterX=189.124 CenterY=124.221 CenterZ=0 NormalX=0 NormalY=0 NormalZ=1 AngleXU=0 Radius=1
    g162: Circle CenterX=185.124 CenterY=124.221 CenterZ=0 NormalX=0 NormalY=0 NormalZ=1 AngleXU=0 Radius=1
    g163: Circle CenterX=185.124 CenterY=120.221 CenterZ=0 NormalX=0 NormalY=0 NormalZ=1 AngleXU=0 Radius=1
    g164: BSplineCurve PolesCount=3 KnotsCount=2 Degree=2 IsPeriodic=0
    g165: GeomPoint X=189.124 Y=124.221 Z=0
    g166: GeomPoint X=185.124 Y=120.221 Z=0
    g167: Circle CenterX=175.022 CenterY=124.221 CenterZ=0 NormalX=0 NormalY=0 NormalZ=1 AngleXU=0 Radius=1
    g168: Circle CenterX=179.022 CenterY=124.221 CenterZ=0 NormalX=0 NormalY=0 NormalZ=1 AngleXU=0 Radius=1
    g169: Circle CenterX=179.022 CenterY=120.221 CenterZ=0 NormalX=0 NormalY=0 NormalZ=1 AngleXU=0 Radius=1
    g170: BSplineCurve PolesCount=3 KnotsCount=2 Degree=2 IsPeriodic=0
    g171: GeomPoint X=175.022 Y=124.221 Z=0
    g172: GeomPoint X=179.022 Y=120.221 Z=0
    g173: Circle CenterX=62.0728 CenterY=124.221 CenterZ=0 NormalX=0 NormalY=0 NormalZ=1 AngleXU=0 Radius=1
    g174: Circle CenterX=58.0728 CenterY=124.221 CenterZ=0 NormalX=0 NormalY=0 NormalZ=1 AngleXU=0 Radius=1
    g175: Circle CenterX=61.1496 CenterY=121.665 CenterZ=0 NormalX=0 NormalY=0 NormalZ=1 AngleXU=0 Radius=1
    g176: BSplineCurve PolesCount=3 KnotsCount=2 Degree=2 IsPeriodic=0
    g177: GeomPoint X=62.0728 Y=124.221 Z=0
    g178: GeomPoint X=61.1496 Y=121.665 Z=0
    g179: LineSegment StartX=179.022 StartY=120.221 StartZ=0 EndX=179.022 EndY=27.0628 EndZ=0
    g180: LineSegment StartX=185.124 StartY=27.0628 StartZ=0 EndX=185.124 EndY=120.221 EndZ=0
    g181: LineSegment StartX=302.996 StartY=121.665 StartZ=0 EndX=189.124 EndY=27.0628 EndZ=0
    g182: LineSegment StartX=175.022 StartY=27.0628 StartZ=0 EndX=61.1496 EndY=121.665 EndZ=0
    g183: Circle CenterX=61.5791 CenterY=75.4095 CenterZ=0 NormalX=0 NormalY=0 NormalZ=1 AngleXU=0 Radius=1
    g184: Circle CenterX=58.0728 CenterY=77.3346 CenterZ=0 NormalX=0 NormalY=0 NormalZ=1 AngleXU=0 Radius=1
    g185: Circle CenterX=58.0728 CenterY=73.3346 CenterZ=0 NormalX=0 NormalY=0 NormalZ=1 AngleXU=0 Radius=1
    g186: BSplineCurve PolesCount=3 KnotsCount=2 Degree=2 IsPeriodic=0
    g187: GeomPoint X=61.5791 Y=75.4095 Z=0
    g188: GeomPoint X=58.0728 Y=73.3346 Z=0
    g189: Circle CenterX=58.0728 CenterY=-40.8935 CenterZ=0 NormalX=0 NormalY=0 NormalZ=1 AngleXU=0 Radius=1
    g190: Circle CenterX=58.0728 CenterY=-44.8935 CenterZ=0 NormalX=0 NormalY=0 NormalZ=1 AngleXU=0 Radius=1
    g191: Circle CenterX=61.5791 CenterY=-42.9683 CenterZ=0 NormalX=0 NormalY=0 NormalZ=1 AngleXU=0 Radius=1
    g192: BSplineCurve PolesCount=3 KnotsCount=2 Degree=2 IsPeriodic=0
    g193: GeomPoint X=58.0728 Y=-40.8935 Z=0
    g194: GeomPoint X=61.5791 Y=-42.9683 Z=0
    g195: LineSegment StartX=61.5791 StartY=-42.9683 StartZ=0 EndX=165.871 EndY=14.2954 EndZ=0
    g196: LineSegment StartX=165.871 StartY=18.1458 StartZ=0 EndX=61.5791 EndY=75.4095 EndZ=0
    g197: LineSegment StartX=58.0728 StartY=73.3346 StartZ=0 EndX=58.0728 EndY=-40.8935 EndZ=0
    g198: Circle CenterX=302.567 CenterY=-42.9683 CenterZ=0 NormalX=0 NormalY=0 NormalZ=1 AngleXU=0 Radius=1
    g199: Circle CenterX=306.073 CenterY=-44.8935 CenterZ=0 NormalX=0 NormalY=0 NormalZ=1 AngleXU=0 Radius=1
    g200: Circle CenterX=306.073 CenterY=-40.8935 CenterZ=0 NormalX=0 NormalY=0 NormalZ=1 AngleXU=0 Radius=1
    g201: BSplineCurve PolesCount=3 KnotsCount=2 Degree=2 IsPeriodic=0
    g202: GeomPoint X=302.567 Y=-42.9683 Z=0
    g203: GeomPoint X=306.073 Y=-40.8935 Z=0
    g204: Circle CenterX=306.073 CenterY=73.3346 CenterZ=0 NormalX=0 NormalY=0 NormalZ=1 AngleXU=0 Radius=1
    g205: Circle CenterX=306.073 CenterY=77.3346 CenterZ=0 NormalX=0 NormalY=0 NormalZ=1 AngleXU=0 Radius=1
    g206: Circle CenterX=302.567 CenterY=75.4095 CenterZ=0 NormalX=0 NormalY=0 NormalZ=1 AngleXU=0 Radius=1
    g207: BSplineCurve PolesCount=3 KnotsCount=2 Degree=2 IsPeriodic=0
    g208: GeomPoint X=306.073 Y=73.3346 Z=0
    g209: GeomPoint X=302.567 Y=75.4095 Z=0
    g210: LineSegment StartX=302.567 StartY=-42.9683 StartZ=0 EndX=198.275 EndY=14.2954 EndZ=0
    g211: LineSegment StartX=198.275 StartY=18.1458 StartZ=0 EndX=302.567 EndY=75.4095 EndZ=0
    g212: LineSegment StartX=306.073 StartY=73.3346 StartZ=0 EndX=306.073 EndY=-40.8935 EndZ=0
    g213: LineSegment StartX=322.073 StartY=105.865 StartZ=0 EndX=328.643 EndY=105.865 EndZ=0
    g214: LineSegment StartX=318.073 StartY=120.221 StartZ=0 EndX=318.073 EndY=109.865 EndZ=0
    g215: LineSegment StartX=336.157 StartY=107.779 StartZ=0 EndX=362.567 EndY=122.294 EndZ=0
    g216: Circle CenterX=362.073 CenterY=124.221 CenterZ=0 NormalX=0 NormalY=0 NormalZ=1 AngleXU=0 Radius=1
    g217: Circle CenterX=366.073 CenterY=124.221 CenterZ=0 NormalX=0 NormalY=0 NormalZ=1 AngleXU=0 Radius=1
    g218: Circle CenterX=362.567 CenterY=122.294 CenterZ=0 NormalX=0 NormalY=0 NormalZ=1 AngleXU=0 Radius=1
    g219: BSplineCurve PolesCount=3 KnotsCount=2 Degree=2 IsPeriodic=0
    g220: GeomPoint X=362.073 Y=124.221 Z=0
    g221: GeomPoint X=362.567 Y=122.294 Z=0
    g222: Circle CenterX=322.073 CenterY=124.221 CenterZ=0 NormalX=0 NormalY=0 NormalZ=1 AngleXU=0 Radius=1
    g223: Circle CenterX=318.073 CenterY=124.221 CenterZ=0 NormalX=0 NormalY=0 NormalZ=1 AngleXU=0 Radius=1
    g224: Circle CenterX=318.073 CenterY=120.221 CenterZ=0 NormalX=0 NormalY=0 NormalZ=1 AngleXU=0 Radius=1
    g225: BSplineCurve PolesCount=3 KnotsCount=2 Degree=2 IsPeriodic=0
    g226: GeomPoint X=322.073 Y=124.221 Z=0
    g227: GeomPoint X=318.073 Y=120.221 Z=0
    g228: Circle CenterX=322.073 CenterY=105.865 CenterZ=0 NormalX=0 NormalY=0 NormalZ=1 AngleXU=0 Radius=1
    g229: Circle CenterX=318.073 CenterY=105.865 CenterZ=0 NormalX=0 NormalY=0 NormalZ=1 AngleXU=0 Radius=1
    g230: Circle CenterX=318.073 CenterY=109.865 CenterZ=0 NormalX=0 NormalY=0 NormalZ=1 AngleXU=0 Radius=1
    g231: BSplineCurve PolesCount=3 KnotsCount=2 Degree=2 IsPeriodic=0
    g232: GeomPoint X=322.073 Y=105.865 Z=0
    g233: GeomPoint X=318.073 Y=109.865 Z=0
    g234: Circle CenterX=336.157 CenterY=107.779 CenterZ=0 NormalX=0 NormalY=0 NormalZ=1 AngleXU=0 Radius=1
    g235: Circle CenterX=332.651 CenterY=105.853 CenterZ=0 NormalX=0 NormalY=0 NormalZ=1 AngleXU=0 Radius=1
    g236: Circle CenterX=328.643 CenterY=105.865 CenterZ=0 NormalX=0 NormalY=0 NormalZ=1 AngleXU=0 Radius=1
    g237: BSplineCurve PolesCount=3 KnotsCount=2 Degree=2 IsPeriodic=0
    g238: GeomPoint X=336.157 Y=107.779 Z=0
    g239: GeomPoint X=328.643 Y=105.865 Z=0
    g240: LineSegment StartX=322.073 StartY=124.221 StartZ=0 EndX=362.073 EndY=124.221 EndZ=0
    g241: Circle CenterX=371.567 CenterY=-80.8644 CenterZ=0 NormalX=0 NormalY=0 NormalZ=1 AngleXU=0 Radius=1
    g242: Circle CenterX=375.073 CenterY=-82.7896 CenterZ=0 NormalX=0 NormalY=0 NormalZ=1 AngleXU=0 Radius=1
    g243: Circle CenterX=375.073 CenterY=-78.7896 CenterZ=0 NormalX=0 NormalY=0 NormalZ=1 AngleXU=0 Radius=1
    g244: BSplineCurve PolesCount=3 KnotsCount=2 Degree=2 IsPeriodic=0
    g245: GeomPoint X=371.567 Y=-80.8644 Z=0
    g246: GeomPoint X=375.073 Y=-78.7896 Z=0
    g247: Circle CenterX=321.579 CenterY=-53.4075 CenterZ=0 NormalX=0 NormalY=0 NormalZ=1 AngleXU=0 Radius=1
    g248: Circle CenterX=318.073 CenterY=-51.4823 CenterZ=0 NormalX=0 NormalY=0 NormalZ=1 AngleXU=0 Radius=1
    g249: Circle CenterX=318.073 CenterY=-47.4805 CenterZ=0 NormalX=0 NormalY=0 NormalZ=1 AngleXU=0 Radius=1
    g250: BSplineCurve PolesCount=3 KnotsCount=2 Degree=2 IsPeriodic=0
    g251: GeomPoint X=321.579 Y=-53.4075 Z=0
    g252: GeomPoint X=318.073 Y=-47.4805 Z=0
    g253: LineSegment StartX=371.567 StartY=-80.8644 StartZ=0 EndX=321.579 EndY=-53.4075 EndZ=0
    g254: Circle CenterX=321.579 CenterY=-67.3492 CenterZ=0 NormalX=0 NormalY=0 NormalZ=1 AngleXU=0 Radius=1
    g255: Circle CenterX=318.073 CenterY=-65.424 CenterZ=0 NormalX=0 NormalY=0 NormalZ=1 AngleXU=0 Radius=1
    g256: Circle CenterX=318.073 CenterY=-69.424 CenterZ=0 NormalX=0 NormalY=0 NormalZ=1 AngleXU=0 Radius=1
    g257: BSplineCurve PolesCount=3 KnotsCount=2 Degree=2 IsPeriodic=0
    g258: GeomPoint X=321.579 Y=-67.3492 Z=0
    g259: GeomPoint X=318.073 Y=-69.424 Z=0
    g260: Circle CenterX=362.567 CenterY=-89.8542 CenterZ=0 NormalX=0 NormalY=0 NormalZ=1 AngleXU=0 Radius=1
    g261: Circle CenterX=366.073 CenterY=-91.7794 CenterZ=0 NormalX=0 NormalY=0 NormalZ=1 AngleXU=0 Radius=1
    g262: Circle CenterX=362.073 CenterY=-91.7794 CenterZ=0 NormalX=0 NormalY=0 NormalZ=1 AngleXU=0 Radius=1
    g263: BSplineCurve PolesCount=3 KnotsCount=2 Degree=2 IsPeriodic=0
    g264: GeomPoint X=362.567 Y=-89.8542 Z=0
    g265: GeomPoint X=362.073 Y=-91.7794 Z=0
    g266: Circle CenterX=322.073 CenterY=-91.7794 CenterZ=0 NormalX=0 NormalY=0 NormalZ=1 AngleXU=0 Radius=1
    g267: Circle CenterX=318.073 CenterY=-91.7794 CenterZ=0 NormalX=0 NormalY=0 NormalZ=1 AngleXU=0 Radius=1
    g268: Circle CenterX=318.073 CenterY=-87.7794 CenterZ=0 NormalX=0 NormalY=0 NormalZ=1 AngleXU=0 Radius=1
    g269: BSplineCurve PolesCount=3 KnotsCount=2 Degree=2 IsPeriodic=0
    g270: GeomPoint X=322.073 Y=-91.7794 Z=0
    g271: GeomPoint X=318.073 Y=-87.7794 Z=0
    g272: LineSegment StartX=362.567 StartY=-89.8542 StartZ=0 EndX=321.579 EndY=-67.3492 EndZ=0
    g273: LineSegment StartX=318.073 StartY=-69.424 StartZ=0 EndX=318.073 EndY=-87.7794 EndZ=0
    g274: LineSegment StartX=322.073 StartY=-91.7794 StartZ=0 EndX=362.073 EndY=-91.7794 EndZ=0
    g275: Circle CenterX=2.07281 CenterY=124.221 CenterZ=0 NormalX=0 NormalY=0 NormalZ=1 AngleXU=0 Radius=1
    g276: Circle CenterX=1.57905 CenterY=122.295 CenterZ=0 NormalX=0 NormalY=0 NormalZ=1 AngleXU=0 Radius=1
    g277: BSplineCurve PolesCount=3 KnotsCount=2 Degree=2 IsPeriodic=0
    g278: GeomPoint X=2.07281 Y=124.221 Z=0
    g279: GeomPoint X=1.57905 Y=122.295 Z=0
    g280: Circle CenterX=42.0728 CenterY=124.221 CenterZ=0 NormalX=0 NormalY=0 NormalZ=1 AngleXU=0 Radius=1
    g281: Circle CenterX=46.0728 CenterY=124.221 CenterZ=0 NormalX=0 NormalY=0 NormalZ=1 AngleXU=0 Radius=1
    g282: Circle CenterX=46.0728 CenterY=120.221 CenterZ=0 NormalX=0 NormalY=0 NormalZ=1 AngleXU=0 Radius=1
    g283: BSplineCurve PolesCount=3 KnotsCount=2 Degree=2 IsPeriodic=0
    g284: GeomPoint X=42.0728 Y=124.221 Z=0
    g285: GeomPoint X=46.0728 Y=120.221 Z=0
    g286: Circle CenterX=46.0728 CenterY=109.865 CenterZ=0 NormalX=0 NormalY=0 NormalZ=1 AngleXU=0 Radius=1
    g287: Circle CenterX=46.0728 CenterY=105.865 CenterZ=0 NormalX=0 NormalY=0 NormalZ=1 AngleXU=0 Radius=1
    g288: Circle CenterX=42.0728 CenterY=105.865 CenterZ=0 NormalX=0 NormalY=0 NormalZ=1 AngleXU=0 Radius=1
    g289: BSplineCurve PolesCount=3 KnotsCount=2 Degree=2 IsPeriodic=0
    g290: GeomPoint X=46.0728 Y=109.865 Z=0
    g291: GeomPoint X=42.0728 Y=105.865 Z=0
    g292: Circle CenterX=35.5028 CenterY=105.865 CenterZ=0 NormalX=0 NormalY=0 NormalZ=1 AngleXU=0 Radius=1
    g293: Circle CenterX=31.5028 CenterY=105.865 CenterZ=0 NormalX=0 NormalY=0 NormalZ=1 AngleXU=0 Radius=1
    g294: Circle CenterX=27.9965 CenterY=107.79 CenterZ=0 NormalX=0 NormalY=0 NormalZ=1 AngleXU=0 Radius=1
    g295: BSplineCurve PolesCount=3 KnotsCount=2 Degree=2 IsPeriodic=0
    g296: GeomPoint X=35.5028 Y=105.865 Z=0
    g297: GeomPoint X=27.9965 Y=107.79 Z=0
    g298: LineSegment StartX=2.07281 StartY=124.221 StartZ=0 EndX=42.0728 EndY=124.221 EndZ=0
    g299: LineSegment StartX=46.0728 StartY=120.221 StartZ=0 EndX=46.0728 EndY=109.865 EndZ=0
    g300: LineSegment StartX=42.0728 StartY=105.865 StartZ=0 EndX=35.5028 EndY=105.865 EndZ=0
    g301: LineSegment StartX=27.9965 StartY=107.79 StartZ=0 EndX=1.57905 EndY=122.295 EndZ=0
    g302: Circle CenterX=42.5666 CenterY=-67.3492 CenterZ=0 NormalX=0 NormalY=0 NormalZ=1 AngleXU=0 Radius=1
    g303: Circle CenterX=46.0728 CenterY=-65.424 CenterZ=0 NormalX=0 NormalY=0 NormalZ=1 AngleXU=0 Radius=1
    g304: Circle CenterX=46.0728 CenterY=-69.424 CenterZ=0 NormalX=0 NormalY=0 NormalZ=1 AngleXU=0 Radius=1
    g305: BSplineCurve PolesCount=3 KnotsCount=2 Degree=2 IsPeriodic=0
    g306: GeomPoint X=42.5666 Y=-67.3492 Z=0
    g307: GeomPoint X=46.0728 Y=-69.424 Z=0
    g308: Circle CenterX=46.0728 CenterY=-87.7794 CenterZ=0 NormalX=0 NormalY=0 NormalZ=1 AngleXU=0 Radius=1
    g309: Circle CenterX=46.0728 CenterY=-91.7794 CenterZ=0 NormalX=0 NormalY=0 NormalZ=1 AngleXU=0 Radius=1
    g310: Circle CenterX=42.0728 CenterY=-91.7794 CenterZ=0 NormalX=0 NormalY=0 NormalZ=1 AngleXU=0 Radius=1
    g311: BSplineCurve PolesCount=3 KnotsCount=2 Degree=2 IsPeriodic=0
    g312: GeomPoint X=46.0728 Y=-87.7794 Z=0
    g313: GeomPoint X=42.0728 Y=-91.7794 Z=0
    g314: Circle CenterX=2.07281 CenterY=-91.7794 CenterZ=0 NormalX=0 NormalY=0 NormalZ=1 AngleXU=0 Radius=1
    g315: Circle CenterX=-1.92719 CenterY=-91.7794 CenterZ=0 NormalX=0 NormalY=0 NormalZ=1 AngleXU=0 Radius=1
    g316: Circle CenterX=1.57905 CenterY=-89.8542 CenterZ=0 NormalX=0 NormalY=0 NormalZ=1 AngleXU=0 Radius=1
    g317: BSplineCurve PolesCount=3 KnotsCount=2 Degree=2 IsPeriodic=0
    g318: GeomPoint X=2.07281 Y=-91.7794 Z=0
    g319: GeomPoint X=1.57905 Y=-89.8542 Z=0
    g320: LineSegment StartX=2.07281 StartY=-91.7794 StartZ=0 EndX=42.0728 EndY=-91.7794 EndZ=0
    g321: LineSegment StartX=46.0728 StartY=-87.7794 StartZ=0 EndX=46.0728 EndY=-69.424 EndZ=0
    g322: LineSegment StartX=42.5666 StartY=-67.3492 StartZ=0 EndX=1.57905 EndY=-89.8542 EndZ=0
    g323: Circle CenterX=322.073 CenterY=76.4095 CenterZ=0 NormalX=0 NormalY=0 NormalZ=1 AngleXU=0 Radius=4
    g324: BSplineCurve PolesCount=3 KnotsCount=2 Degree=2 IsPeriodic=0
    g325: GeomPoint X=318.073 Y=72.4095 Z=0
    g326: GeomPoint X=322.073 Y=76.4095 Z=0
    g327: Circle CenterX=375.073 CenterY=72.4095 CenterZ=0 NormalX=0 NormalY=0 NormalZ=1 AngleXU=0 Radius=1
    g328: Circle CenterX=375.073 CenterY=76.4095 CenterZ=0 NormalX=0 NormalY=0 NormalZ=1 AngleXU=0 Radius=1
    g329: Circle CenterX=371.073 CenterY=76.4095 CenterZ=0 NormalX=0 NormalY=0 NormalZ=1 AngleXU=0 Radius=1
    g330: BSplineCurve PolesCount=3 KnotsCount=2 Degree=2 IsPeriodic=0
    g331: GeomPoint X=375.073 Y=72.4095 Z=0
    g332: GeomPoint X=371.073 Y=76.4095 Z=0
    g333: LineSegment StartX=322.073 StartY=76.4095 StartZ=0 EndX=371.073 EndY=76.4095 EndZ=0
    g334: LineSegment StartX=318.073 StartY=72.4095 StartZ=0 EndX=318.073 EndY=-47.4805 EndZ=0
    g335: LineSegment StartX=375.073 StartY=72.4095 StartZ=0 EndX=375.073 EndY=-78.7896 EndZ=0
    g336: ArcOfCircle CenterX=-26.9272 CenterY=22.1087 CenterZ=0 NormalX=0 NormalY=0 NormalZ=1 AngleXU=0 Radius=4 StartAngle=5e-16 EndAngle=3.14159
    g337: LineSegment StartX=-22.9272 StartY=22.1087 StartZ=0 EndX=-18.9272 EndY=-83.7794 EndZ=0
    g338: LineSegment StartX=-34.9272 StartY=-83.7794 StartZ=0 EndX=-30.9272 EndY=22.1087 EndZ=0
    g339: ArcOfCircle CenterX=391.073 CenterY=22.1087 CenterZ=0 NormalX=0 NormalY=0 NormalZ=1 AngleXU=0 Radius=4 StartAngle=0 EndAngle=3.14159
    g340: LineSegment StartX=387.073 StartY=22.1087 StartZ=0 EndX=383.073 EndY=-83.7794 EndZ=0
    g341: LineSegment StartX=395.073 StartY=22.1087 StartZ=0 EndX=399.073 EndY=-83.7794 EndZ=0
    g342: Circle CenterX=-10.9272 CenterY=-78.7794 CenterZ=0 NormalX=0 NormalY=0 NormalZ=1 AngleXU=0 Radius=1
    g343: Circle CenterX=-10.9272 CenterY=-82.7794 CenterZ=0 NormalX=0 NormalY=0 NormalZ=1 AngleXU=0 Radius=1
    g344: Circle CenterX=-7.42095 CenterY=-80.8542 CenterZ=0 NormalX=0 NormalY=0 NormalZ=1 AngleXU=0 Radius=1
    g345: BSplineCurve PolesCount=3 KnotsCount=2 Degree=2 IsPeriodic=0
    g346: GeomPoint X=-10.9272 Y=-78.7794 Z=0
    g347: GeomPoint X=-7.42095 Y=-80.8542 Z=0
    g348: Circle CenterX=42.5666 CenterY=-53.4075 CenterZ=0 NormalX=0 NormalY=0 NormalZ=1 AngleXU=0 Radius=1
    g349: Circle CenterX=46.0728 CenterY=-51.4823 CenterZ=0 NormalX=0 NormalY=0 NormalZ=1 AngleXU=0 Radius=1
    g350: Circle CenterX=46.0728 CenterY=-47.4823 CenterZ=0 NormalX=0 NormalY=0 NormalZ=1 AngleXU=0 Radius=1
    g351: BSplineCurve PolesCount=3 KnotsCount=2 Degree=2 IsPeriodic=0
    g352: GeomPoint X=42.5666 Y=-53.4075 Z=0
    g353: GeomPoint X=46.0728 Y=-47.4823 Z=0
    g354: Circle CenterX=46.0728 CenterY=72.4095 CenterZ=0 NormalX=0 NormalY=0 NormalZ=1 AngleXU=0 Radius=1
    g355: Circle CenterX=46.0728 CenterY=76.4095 CenterZ=0 NormalX=0 NormalY=0 NormalZ=1 AngleXU=0 Radius=1
    g356: Circle CenterX=42.0728 CenterY=76.4095 CenterZ=0 NormalX=0 NormalY=0 NormalZ=1 AngleXU=0 Radius=1
    g357: BSplineCurve PolesCount=3 KnotsCount=2 Degree=2 IsPeriodic=0
    g358: GeomPoint X=46.0728 Y=72.4095 Z=0
    g359: GeomPoint X=42.0728 Y=76.4095 Z=0
    g360: Circle CenterX=-6.92718 CenterY=76.4095 CenterZ=0 NormalX=0 NormalY=0 NormalZ=1 AngleXU=0 Radius=1
    g361: Circle CenterX=-10.9272 CenterY=76.4095 CenterZ=0 NormalX=0 NormalY=0 NormalZ=1 AngleXU=0 Radius=1
    g362: Circle CenterX=-10.9272 CenterY=72.4095 CenterZ=0 NormalX=0 NormalY=0 NormalZ=1 AngleXU=0 Radius=1
    g363: BSplineCurve PolesCount=3 KnotsCount=2 Degree=2 IsPeriodic=0
    g364: GeomPoint X=-6.92718 Y=76.4095 Z=0
    g365: GeomPoint X=-10.9272 Y=72.4095 Z=0
    g366: LineSegment StartX=-10.9272 StartY=72.4095 StartZ=0 EndX=-10.9272 EndY=-78.7794 EndZ=0
    g367: LineSegment StartX=-7.42095 StartY=-80.8542 StartZ=0 EndX=42.5666 EndY=-53.4075 EndZ=0
    g368: LineSegment StartX=46.0728 StartY=-47.4823 StartZ=0 EndX=46.0728 EndY=72.4095 EndZ=0
    g369: LineSegment StartX=42.0728 StartY=76.4095 StartZ=0 EndX=-6.92719 EndY=76.4095 EndZ=0
    g370: LineSegment StartX=245.072 StartY=136.221 StartZ=0 EndX=245.072 EndY=-116.499 EndZ=0
    g371: LineSegment StartX=119.072 StartY=136.221 StartZ=0 EndX=119.072 EndY=-116.228 EndZ=0
    g372: LineSegment StartX=-42.9272 StartY=136.221 StartZ=0 EndX=407.073 EndY=136.221 EndZ=0
    g373: LineSegment StartX=232.072 StartY=136.221 StartZ=0 EndX=220.072 EndY=136.221 EndZ=0
    g374: LineSegment StartX=232.072 StartY=136.221 StartZ=0 EndX=232.072 EndY=124.221 EndZ=0
    g375: LineSegment StartX=220.072 StartY=136.221 StartZ=0 EndX=220.072 EndY=124.221 EndZ=0
    g376: LineSegment StartX=220.072 StartY=136.221 StartZ=0 EndX=226.072 EndY=136.221 EndZ=0
    g377: LineSegment StartX=220.072 StartY=136.221 StartZ=0 EndX=220.072 EndY=130.221 EndZ=0
    g378: LineSegment StartX=220.072 StartY=124.221 StartZ=0 EndX=226.072 EndY=124.221 EndZ=0
    g379: LineSegment StartX=232.072 StartY=124.221 StartZ=0 EndX=232.072 EndY=127.221 EndZ=0
    g380: LineSegment StartX=232.072 StartY=136.221 StartZ=0 EndX=232.072 EndY=133.221 EndZ=0
    g381-g385: Circle x5 (B-spline internal-alignment scaffolding for g386; pole/knot coordinates omitted)
    g386: BSplineCurve PolesCount=5 KnotsCount=3 Degree=3 IsPeriodic=0
    g387: GeomPoint X=232.072 Y=133.221 Z=0
    g388: GeomPoint X=223.072 Y=130.221 Z=0
    g389: GeomPoint X=232.072 Y=127.221 Z=0
    g390: LineSegment StartX=189.124 StartY=124.221 StartZ=0 EndX=302.073 EndY=124.221 EndZ=0
    g391: LineSegment StartX=132.072 StartY=136.221 StartZ=0 EndX=132.072 EndY=124.221 EndZ=0
    g392: LineSegment StartX=132.072 StartY=136.221 StartZ=0 EndX=144.072 EndY=136.221 EndZ=0
    g393: LineSegment StartX=144.072 StartY=136.221 StartZ=0 EndX=144.072 EndY=124.221 EndZ=0
    g394: LineSegment StartX=144.072 StartY=136.221 StartZ=0 EndX=138.072 EndY=136.221 EndZ=0
    g395: LineSegment StartX=144.072 StartY=136.221 StartZ=0 EndX=144.072 EndY=130.221 EndZ=0
    g396: LineSegment StartX=132.072 StartY=136.221 StartZ=0 EndX=132.072 EndY=133.221 EndZ=0
    g397: LineSegment StartX=132.072 StartY=133.221 StartZ=0 EndX=132.072 EndY=127.221 EndZ=0
    g398-g402: Circle x5 (B-spline internal-alignment scaffolding for g403; pole/knot coordinates omitted)
    g403: BSplineCurve PolesCount=5 KnotsCount=3 Degree=3 IsPeriodic=0
    g404: GeomPoint X=132.072 Y=133.221 Z=0
    g405: GeomPoint X=141.072 Y=130.221 Z=0
    g406: GeomPoint X=132.072 Y=127.221 Z=0
    g407: LineSegment StartX=132.072 StartY=124.221 StartZ=0 EndX=175.022 EndY=124.221 EndZ=0
    ... +13 more geometry lines
  constraints (712):
    c: Vertical(g0)
    c: Vertical(g1)
    c: Block(g1)
    c: Block(g0)
    c: Weight(g4) = 1
    c: Equal(g4,g5)
    c: Equal(g4,g6)
    c: InternalAlignment(g4,g7)
    c: InternalAlignment(g5,g7)
    c: InternalAlignment(g6,g7)
    c: InternalAlignment(g8,g7)
    c: InternalAlignment(g9,g7)
    c: Weight(g10) = 1
    c: Equal(g10,g11)
    c: Equal(g10,g12)
    c: InternalAlignment(g10,g13)
    c: InternalAlignment(g11,g13)
    c: InternalAlignment(g12,g13)
    c: InternalAlignment(g14,g13)
    c: InternalAlignment(g15,g13)
    c: Block(g13)
    c: Block(g7)
    c: Weight(g16) = 1
    c: Equal(g16,g17)
    c: Equal(g16,g18)
    c: InternalAlignment(g16,g19)
    c: InternalAlignment(g17,g19)
    c: InternalAlignment(g18,g19)
    c: InternalAlignment(g20,g19)
    c: InternalAlignment(g21,g19)
    c: Weight(g22) = 1
    c: Equal(g22,g23)
    c: Equal(g22,g24)
    c: InternalAlignment(g22,g25)
    c: InternalAlignment(g23,g25)
    c: InternalAlignment(g24,g25)
    c: InternalAlignment(g26,g25)
    c: InternalAlignment(g27,g25)
    c: Block(g25)
    c: Block(g19)
    c: Weight(g28) = 1
    c: Equal(g28,g29)
    c: Equal(g28,g30)
    c: InternalAlignment(g28,g31)
    c: InternalAlignment(g29,g31)
    c: InternalAlignment(g30,g31)
    c: InternalAlignment(g32,g31)
    c: InternalAlignment(g33,g31)
    c: Weight(g34) = 1
    c: Equal(g34,g35)
    c: Equal(g34,g36)
    c: InternalAlignment(g34,g37)
    c: InternalAlignment(g35,g37)
    c: InternalAlignment(g36,g37)
    c: InternalAlignment(g38,g37)
    c: InternalAlignment(g39,g37)
    c: Block(g31)
    c: Block(g37)
    c: Coincident(g40,g1)
    c: Coincident(g40,g0)
    c: Horizontal(g40)
    c: Distance(g40) = 450
    c: Weight(g41) = 1
    c: Equal(g41,g42)
    c: Equal(g41,g43)
    c: InternalAlignment(g41,g44)
    c: InternalAlignment(g42,g44)
    c: InternalAlignment(g43,g44)
    c: InternalAlignment(g45,g44)
    c: InternalAlignment(g46,g44)
    c: Block(g44)
    c: Weight(g47) = 1
    c: Equal(g47,g48)
    c: Equal(g47,g49)
    c: InternalAlignment(g47,g50)
    c: InternalAlignment(g48,g50)
    c: InternalAlignment(g49,g50)
    c: InternalAlignment(g51,g50)
    c: InternalAlignment(g52,g50)
    c: Block(g50)
    c: Weight(g53) = 1
    c: Equal(g53,g54)
    c: Equal(g53,g55)
    c: InternalAlignment(g53,g56)
    c: InternalAlignment(g54,g56)
    c: InternalAlignment(g55,g56)
    c: InternalAlignment(g57,g56)
    c: InternalAlignment(g58,g56)
    c: Block(g56)
    c: Weight(g59) = 1
    c: Equal(g59,g60)
    c: Equal(g59,g61)
    c: InternalAlignment(g59,g62)
    c: InternalAlignment(g60,g62)
    c: InternalAlignment(g61,g62)
    c: InternalAlignment(g63,g62)
    c: InternalAlignment(g64,g62)
    c: Block(g62)
    c: Weight(g65) = 1
    c: Equal(g65,g66)
    c: Equal(g65,g67)
    c: InternalAlignment(g65,g68)
    c: InternalAlignment(g66,g68)
    c: InternalAlignment(g67,g68)
    c: InternalAlignment(g69,g68)
    c: InternalAlignment(g70,g68)
    c: Weight(g71) = 1
    c: Equal(g71,g72)
    c: Equal(g71,g73)
    c: InternalAlignment(g71,g74)
    c: InternalAlignment(g72,g74)
    c: InternalAlignment(g73,g74)
    c: InternalAlignment(g75,g74)
    c: InternalAlignment(g76,g74)
    c: Block(g68)
    c: Block(g74)
    c: Coincident(g77,g68)
    c: Coincident(g77,g74)
    c: Vertical(g77)
    c: Coincident(g78,g68)
    c: Coincident(g78,g50)
    c: Coincident(g79,g50)
    c: Coincident(g79,g74)
    c: Weight(g80) = 1
    c: Equal(g80,g81)
    c: Equal(g80,g82)
    c: InternalAlignment(g80,g83)
    c: InternalAlignment(g81,g83)
    c: InternalAlignment(g82,g83)
    c: InternalAlignment(g84,g83)
    c: InternalAlignment(g85,g83)
    c: Weight(g86) = 1
    c: Equal(g86,g87)
    c: Equal(g86,g88)
    c: InternalAlignment(g86,g89)
    c: InternalAlignment(g87,g89)
    c: InternalAlignment(g88,g89)
    c: InternalAlignment(g90,g89)
    c: InternalAlignment(g91,g89)
    c: Block(g83)
    c: Block(g89)
    c: Coincident(g92,g83)
    c: Coincident(g92,g89)
    c: Vertical(g92)
    c: Coincident(g93,g83)
    c: Coincident(g93,g44)
    c: Coincident(g94,g44)
    c: Coincident(g94,g89)
    c: Weight(g95) = 1
    c: Equal(g95,g96)
    c: Equal(g95,g97)
    c: InternalAlignment(g95,g98)
    c: InternalAlignment(g96,g98)
    c: InternalAlignment(g97,g98)
    c: InternalAlignment(g99,g98)
    c: InternalAlignment(g100,g98)
    c: Weight(g101) = 1
    c: Equal(g101,g102)
    c: Equal(g101,g103)
    c: InternalAlignment(g101,g104)
    c: InternalAlignment(g102,g104)
    c: InternalAlignment(g103,g104)
    c: InternalAlignment(g105,g104)
    c: InternalAlignment(g106,g104)
    c: Block(g98)
    c: Block(g104)
    c: Coincident(g107,g98)
    c: Coincident(g107,g104)
    c: Vertical(g107)
    c: Coincident(g108,g104)
    c: Coincident(g108,g62)
    c: Coincident(g109,g62)
    c: Coincident(g109,g98)
    c: Weight(g110) = 1
    c: Equal(g110,g111)
    c: Equal(g110,g112)
    c: InternalAlignment(g110,g113)
    c: InternalAlignment(g111,g113)
    c: InternalAlignment(g112,g113)
    c: InternalAlignment(g114,g113)
    c: InternalAlignment(g115,g113)
    c: Weight(g116) = 1
    c: Equal(g116,g117)
    c: Equal(g116,g118)
    c: InternalAlignment(g116,g119)
    c: InternalAlignment(g117,g119)
    c: InternalAlignment(g118,g119)
    c: InternalAlignment(g120,g119)
    c: InternalAlignment(g121,g119)
    c: Block(g113)
    c: Block(g119)
    c: Coincident(g122,g113)
    c: Coincident(g122,g119)
    c: Vertical(g122)
    c: Coincident(g123,g119)
    c: Coincident(g123,g56)
    c: Coincident(g124,g56)
    c: Coincident(g124,g113)
    c: Weight(g125) = 1
    c: Equal(g125,g126)
    c: Equal(g125,g127)
    c: InternalAlignment(g125,g128)
    c: InternalAlignment(g126,g128)
    c: InternalAlignment(g127,g128)
    c: InternalAlignment(g129,g128)
    c: InternalAlignment(g130,g128)
    c: Weight(g131) = 1
    c: Equal(g131,g132)
    c: Equal(g131,g133)
    c: InternalAlignment(g131,g134)
    c: InternalAlignment(g132,g134)
    c: InternalAlignment(g133,g134)
    c: InternalAlignment(g135,g134)
    c: InternalAlignment(g136,g134)
    c: Weight(g137) = 1
    c: Equal(g137,g138)
    c: Equal(g137,g139)
    c: InternalAlignment(g137,g140)
    c: InternalAlignment(g138,g140)
    c: InternalAlignment(g139,g140)
    c: InternalAlignment(g141,g140)
    c: InternalAlignment(g142,g140)
    c: Weight(g143) = 1
    c: Equal(g143,g144)
    c: Equal(g143,g145)
    c: InternalAlignment(g143,g146)
    c: InternalAlignment(g144,g146)
    c: InternalAlignment(g145,g146)
    c: InternalAlignment(g147,g146)
    c: InternalAlignment(g148,g146)
    c: Block(g146)
    c: Block(g140)
    c: Block(g134)
    c: Block(g128)
    c: Coincident(g149,g25)
    c: Coincident(g149,g146)
    c: Coincident(g150,g146)
    c: Coincident(g150,g140)
    c: Horizontal(g150)
    c: Coincident(g151,g140)
    c: Coincident(g151,g25)
    c: Vertical(g151)
    c: Coincident(g152,g19)
    c: Coincident(g152,g134)
    c: Vertical(g152)
    c: Coincident(g153,g134)
    c: Coincident(g153,g128)
    c: Horizontal(g153)
    c: Coincident(g154,g128)
    c: Coincident(g154,g19)
    c: Weight(g155) = 1
    c: Equal(g155,g156)
    c: Equal(g155,g157)
    c: InternalAlignment(g155,g158)
    c: InternalAlignment(g156,g158)
    c: InternalAlignment(g157,g158)
    c: InternalAlignment(g159,g158)
    c: InternalAlignment(g160,g158)
    c: Weight(g161) = 1
    c: Equal(g161,g162)
    c: Equal(g161,g163)
    c: InternalAlignment(g161,g164)
    c: InternalAlignment(g162,g164)
    c: InternalAlignment(g163,g164)
    c: InternalAlignment(g165,g164)
    c: InternalAlignment(g166,g164)
    c: Weight(g167) = 1
    c: Equal(g167,g168)
    c: Equal(g167,g169)
    c: InternalAlignment(g167,g170)
    c: InternalAlignment(g168,g170)
    c: InternalAlignment(g169,g170)
    c: InternalAlignment(g171,g170)
    c: InternalAlignment(g172,g170)
    c: Weight(g173) = 1
    c: Equal(g173,g174)
    c: Equal(g173,g175)
    c: InternalAlignment(g173,g176)
    c: InternalAlignment(g174,g176)
    c: InternalAlignment(g175,g176)
    c: InternalAlignment(g177,g176)
    c: InternalAlignment(g178,g176)
    c: Block(g176)
    c: Block(g170)
    c: Block(g164)
    c: Block(g158)
    c: Coincident(g179,g170)
    c: Coincident(g179,g7)
    c: Vertical(g179)
    c: Coincident(g180,g13)
    c: Coincident(g180,g164)
    c: Vertical(g180)
    c: Coincident(g181,g158)
    c: Coincident(g181,g13)
    c: Coincident(g182,g7)
    c: Weight(g183) = 1
    c: Equal(g183,g184)
    c: Equal(g183,g185)
    c: InternalAlignment(g183,g186)
    c: InternalAlignment(g184,g186)
    c: InternalAlignment(g185,g186)
    c: InternalAlignment(g187,g186)
    c: InternalAlignment(g188,g186)
    c: Weight(g189) = 1
    c: Equal(g189,g190)
    c: Equal(g189,g191)
    c: InternalAlignment(g189,g192)
    c: InternalAlignment(g190,g192)
    c: InternalAlignment(g191,g192)
    c: InternalAlignment(g193,g192)
    c: InternalAlignment(g194,g192)
    c: Block(g192)
    c: Block(g186)
    c: Coincident(g195,g192)
    c: Coincident(g195,g31)
    c: Coincident(g196,g31)
    c: Coincident(g196,g186)
    c: Coincident(g197,g186)
    c: Coincident(g197,g192)
    c: Vertical(g197)
    c: Weight(g198) = 1
    c: Equal(g198,g199)
    c: Equal(g198,g200)
    c: InternalAlignment(g198,g201)
    c: InternalAlignment(g199,g201)
    c: InternalAlignment(g200,g201)
    c: InternalAlignment(g202,g201)
    c: InternalAlignment(g203,g201)
    c: Weight(g204) = 1
    c: Equal(g204,g205)
    c: Equal(g204,g206)
    c: InternalAlignment(g204,g207)
    c: InternalAlignment(g205,g207)
    c: InternalAlignment(g206,g207)
    c: InternalAlignment(g208,g207)
    c: InternalAlignment(g209,g207)
    c: Block(g207)
    c: Block(g201)
    c: Coincident(g210,g201)
    c: Coincident(g210,g37)
    c: Coincident(g211,g37)
    c: Coincident(g211,g207)
    c: Coincident(g212,g207)
    c: Coincident(g212,g201)
    c: Vertical(g212)
    c: Horizontal(g213)
    c: Block(g213)
    c: Vertical(g214)
    c: Block(g214)
    c: Block(g215)
    c: Weight(g216) = 1
    c: Equal(g216,g217)
    c: Equal(g216,g218)
    c: InternalAlignment(g216,g219)
    c: InternalAlignment(g217,g219)
    c: InternalAlignment(g218,g219)
    c: InternalAlignment(g220,g219)
    c: InternalAlignment(g221,g219)
    c: Weight(g222) = 1
    c: Equal(g222,g223)
    c: Equal(g222,g224)
    c: InternalAlignment(g222,g225)
    c: InternalAlignment(g223,g225)
    c: InternalAlignment(g224,g225)
    c: InternalAlignment(g226,g225)
    c: InternalAlignment(g227,g225)
    c: Weight(g228) = 1
    c: Equal(g228,g229)
    c: Equal(g228,g230)
    c: InternalAlignment(g228,g231)
    c: InternalAlignment(g229,g231)
    c: InternalAlignment(g230,g231)
    c: InternalAlignment(g232,g231)
    c: InternalAlignment(g233,g231)
    c: Weight(g234) = 1
    c: Equal(g234,g235)
    c: Equal(g234,g236)
    c: InternalAlignment(g234,g237)
    c: InternalAlignment(g235,g237)
    c: InternalAlignment(g236,g237)
    c: InternalAlignment(g238,g237)
    c: InternalAlignment(g239,g237)
    c: Block(g219)
    c: Block(g225)
    c: Block(g231)
    c: Block(g237)
    c: Coincident(g240,g225)
    c: Coincident(g240,g219)
    c: Horizontal(g240)
    c: Block(g182)
    c: Weight(g241) = 1
    c: Equal(g241,g242)
    c: Equal(g241,g243)
    c: InternalAlignment(g241,g244)
    c: InternalAlignment(g242,g244)
    c: InternalAlignment(g243,g244)
    c: InternalAlignment(g245,g244)
    c: InternalAlignment(g246,g244)
    c: Weight(g247) = 1
    c: Equal(g247,g248)
    c: Equal(g247,g249)
    c: InternalAlignment(g247,g250)
    c: InternalAlignment(g248,g250)
    c: InternalAlignment(g249,g250)
    c: InternalAlignment(g251,g250)
    c: InternalAlignment(g252,g250)
    c: Block(g244)
    c: Block(g250)
    c: Coincident(g253,g244)
    c: Coincident(g253,g250)
    c: Weight(g254) = 1
    c: Equal(g254,g255)
    c: Equal(g254,g256)
    c: InternalAlignment(g254,g257)
    c: InternalAlignment(g255,g257)
    c: InternalAlignment(g256,g257)
    c: InternalAlignment(g258,g257)
    c: InternalAlignment(g259,g257)
    c: Weight(g260) = 1
    c: Equal(g260,g261)
    c: Equal(g260,g262)
    c: InternalAlignment(g260,g263)
    c: InternalAlignment(g261,g263)
    c: InternalAlignment(g262,g263)
    c: InternalAlignment(g264,g263)
    c: InternalAlignment(g265,g263)
    c: Weight(g266) = 1
    c: Equal(g266,g267)
    c: Equal(g266,g268)
    c: InternalAlignment(g266,g269)
    c: InternalAlignment(g267,g269)
    c: InternalAlignment(g268,g269)
    c: InternalAlignment(g270,g269)
    c: InternalAlignment(g271,g269)
    c: Block(g269)
    c: Block(g263)
    c: Block(g257)
    c: Coincident(g272,g263)
    c: Coincident(g272,g257)
    c: Coincident(g273,g257)
    c: Coincident(g273,g269)
    c: Vertical(g273)
    c: Coincident(g274,g269)
    c: Coincident(g274,g263)
    c: Horizontal(g274)
    c: Weight(g275) = 1
    c: Equal(g275,g276)
    c: InternalAlignment(g275,g277)
    c: InternalAlignment(g276,g277)
    c: InternalAlignment(g278,g277)
    c: InternalAlignment(g279,g277)
    c: Weight(g280) = 1
    c: InternalAlignment(g281,g283)
    c: InternalAlignment(g282,g283)
    c: InternalAlignment(g284,g283)
    c: InternalAlignment(g285,g283)
    c: Weight(g286) = 1
    c: Equal(g286,g287)
    c: Equal(g286,g288)
    c: InternalAlignment(g286,g289)
    c: InternalAlignment(g287,g289)
    c: InternalAlignment(g288,g289)
    c: InternalAlignment(g290,g289)
    c: InternalAlignment(g291,g289)
    c: Equal(g292,g293)
    c: Equal(g292,g294)
    c: InternalAlignment(g292,g295)
    c: InternalAlignment(g293,g295)
    c: InternalAlignment(g294,g295)
    c: InternalAlignment(g296,g295)
    c: InternalAlignment(g297,g295)
    c: Block(g283)
    c: Block(g289)
    c: Block(g295)
    c: Block(g277)
    c: Coincident(g298,g277)
    c: Coincident(g298,g283)
    c: Horizontal(g298)
    c: Coincident(g299,g283)
    c: Coincident(g299,g289)
    c: Vertical(g299)
    c: Coincident(g300,g289)
    c: Coincident(g300,g295)
    c: Horizontal(g300)
    c: Coincident(g301,g295)
    c: Coincident(g301,g277)
    c: Weight(g302) = 1
    c: Equal(g302,g303)
    c: Equal(g302,g304)
    c: InternalAlignment(g302,g305)
    c: InternalAlignment(g303,g305)
    c: InternalAlignment(g304,g305)
    c: InternalAlignment(g306,g305)
    c: InternalAlignment(g307,g305)
    c: Weight(g308) = 1
    c: Equal(g308,g309)
    c: Equal(g308,g310)
    c: InternalAlignment(g308,g311)
    c: InternalAlignment(g309,g311)
    c: InternalAlignment(g310,g311)
    c: InternalAlignment(g312,g311)
    c: Weight(g314) = 1
    c: Equal(g314,g315)
    c: Equal(g314,g316)
    c: InternalAlignment(g314,g317)
    c: InternalAlignment(g315,g317)
    c: InternalAlignment(g316,g317)
    c: InternalAlignment(g318,g317)
    c: InternalAlignment(g319,g317)
    c: Block(g317)
    c: Block(g311)
    c: Block(g305)
    c: Coincident(g320,g317)
    c: Coincident(g320,g311)
    c: Horizontal(g320)
    c: Coincident(g321,g311)
    c: Coincident(g321,g305)
    c: Vertical(g321)
    c: Coincident(g322,g305)
    c: Coincident(g322,g317)
    c: InternalAlignment(g323,g324)
    c: InternalAlignment(g325,g324)
    c: InternalAlignment(g326,g324)
    c: Block(g324)
    c: Equal(g327,g328)
    c: Equal(g327,g329)
    c: InternalAlignment(g327,g330)
    c: InternalAlignment(g328,g330)
    c: InternalAlignment(g329,g330)
    c: InternalAlignment(g331,g330)
    c: InternalAlignment(g332,g330)
    c: Block(g330)
    c: Coincident(g333,g324)
    c: Horizontal(g333)
    c: Block(g333)
    c: Coincident(g334,g324)
    c: Coincident(g334,g250)
    c: Vertical(g334)
    c: Coincident(g335,g330)
    c: Coincident(g335,g244)
    c: Vertical(g335)
    c: Block(g336)
    c: Block(g2)
    c: Distance(g334) = 119.89
    c: Coincident(g337,g336)
    c: Coincident(g337,g2)
    c: Coincident(g338,g2)
    c: Coincident(g338,g336)
    c: Block(g3)
    c: Block(g339)
    c: Coincident(g340,g339)
    c: Coincident(g340,g3)
    c: Coincident(g341,g339)
    c: Coincident(g341,g3)
    c: Block(g341)
    c: Block(g340)
    c: Weight(g342) = 1
    c: Equal(g342,g343)
    c: Equal(g342,g344)
    c: InternalAlignment(g342,g345)
    c: InternalAlignment(g343,g345)
    c: InternalAlignment(g344,g345)
    c: InternalAlignment(g346,g345)
    c: InternalAlignment(g347,g345)
    c: Weight(g348) = 1
    c: Equal(g348,g349)
    c: Equal(g348,g350)
    c: InternalAlignment(g348,g351)
    c: InternalAlignment(g349,g351)
    c: InternalAlignment(g350,g351)
    c: InternalAlignment(g352,g351)
    c: InternalAlignment(g353,g351)
    c: Weight(g354) = 1
    c: Equal(g354,g355)
    c: Equal(g354,g356)
    c: InternalAlignment(g354,g357)
    c: InternalAlignment(g355,g357)
    c: InternalAlignment(g356,g357)
    c: InternalAlignment(g358,g357)
    c: InternalAlignment(g359,g357)
    c: Weight(g360) = 1
    c: Equal(g360,g361)
    c: Equal(g360,g362)
    c: InternalAlignment(g360,g363)
    c: InternalAlignment(g361,g363)
    c: InternalAlignment(g362,g363)
    c: InternalAlignment(g364,g363)
    c: InternalAlignment(g365,g363)
    c: Block(g363)
    c: Block(g357)
    c: Block(g351)
    c: Block(g345)
    c: Coincident(g366,g363)
    c: Coincident(g366,g345)
    c: Vertical(g366)
    c: Coincident(g367,g345)
    c: Coincident(g367,g351)
    c: Coincident(g368,g351)
    c: Coincident(g368,g357)
    c: Vertical(g368)
    c: Coincident(g369,g357)
    c: Coincident(g369,g363)
    c: Horizontal(g369)
    c: Vertical(g370)
    c: Vertical(g371)
    c: Coincident(g372,g0)
    c: Coincident(g372,g1)
    c: Horizontal(g372)
    c: Block(g372)
    c: Distance(g372) = 450
    c: Block(g370)
    c: Block(g371)
    c: Distance(g0) = 240
    c: Horizontal(g373)
    c: Distance(g373) = 12
    c: Vertical(g374)
    c: Distance(g374) = 12
    c: Coincident(g375,g373)
    c: Vertical(g375)
    c: Horizontal(g376)
    c: Vertical(g377)
    c: Distance(g377) = 6
    c: Coincident(g377,g373)
    c: Coincident(g376,g373)
    c: Block(g375)
    c: Coincident(g378,g375)
    c: Horizontal(g378)
    c: Distance(g378) = 6
    c: Vertical(g379)
    c: Distance(g379) = 3
    c: Vertical(g380)
    c: Distance(g380) = 3
    c: Coincident(g374,g379)
    c: Coincident(g386,g380)
    c: Weight(g381) = 1
    c: Equal(g381,g382)
    c: Coincident(g382,g376)
    c: Equal(g381,g383)
    c: Coincident(g383,g377)
    c: Equal(g381,g384)
    c: Coincident(g384,g378)
    c: Equal(g381,g385)
    c: Coincident(g386,g379)
    c: InternalAlignment(g381-g385 -> g386) x5
    c: InternalAlignment(g387,g386)
    c: InternalAlignment(g388,g386)
    c: InternalAlignment(g389,g386)
    c: Coincident(g390,g164)
    c: Coincident(g390,g158)
    c: Horizontal(g390)
    c: Block(g386)
    c: Vertical(g391)
    c: Distance(g391) = 12
    c: Horizontal(g392)
    c: Distance(g392) = 12
    c: Coincident(g393,g392)
    c: Vertical(g393)
    c: Distance(g393) = 12
    c: Horizontal(g394)
    c: Distance(g394) = 6
    c: Coincident(g394,g392)
    c: Vertical(g395)
    c: Distance(g395) = 6
    c: Coincident(g395,g392)
    c: Vertical(g396)
    c: Distance(g396) = 3
    c: Vertical(g397)
    c: Distance(g397) = 6
    c: Coincident(g397,g396)
    c: Coincident(g403,g396)
    c: Weight(g398) = 1
    c: Equal(g398,g399)
    c: Coincident(g399,g394)
    c: Equal(g398,g400)
    c: Coincident(g400,g395)
    c: Equal(g398,g401)
    c: Equal(g398,g402)
    c: Coincident(g403,g397)
    c: InternalAlignment(g398-g402 -> g403) x5
    c: InternalAlignment(g404,g403)
    c: InternalAlignment(g405,g403)
    c: InternalAlignment(g406,g403)
    c: Coincident(g407,g391)
    c: Coincident(g407,g170)
    c: Horizontal(g407)
    c: Block(g403)
    c: Coincident(g408,g176)
    c: Coincident(g408,g391)
    c: Horizontal(g408)
    c: Block(g407)
    c: Coincident(g410,g391)
    c: PointOnObject(g410,g153)
    c: Vertical(g410)
    c: Block(g411)
    c: Coincident(g412,g411)
    c: Vertical(g412)
    c: PointOnObject(g412,g40)
    c: Block(g412)
    c: Coincident(g413,g411)
    c: Vertical(g413)
    c: Block(g413)
    c: Vertical(g414)
    c: Distance(g414) = 3
    c: Equal(g381,g417) = 1
    c: Equal(g417,g418)
    c: InternalAlignment(g417,g419)
    c: InternalAlignment(g418,g419)
    c: InternalAlignment(g415,g419)
    c: InternalAlignment(g416,g419)
    c: InternalAlignment(g420,g419)
    c: Block(g419)
    c: Coincident(g420,g414)
FEATURE [Part::Extrusion] Extrude005
  Base = -> Sketch003
  Dir = (0,0,1)
  DirMode = 2
  FaceMakerClass = Part::FaceMakerBullseye
  LengthFwd = 24
  LengthRev = 0
  Solid = true
  Symmetric = false
